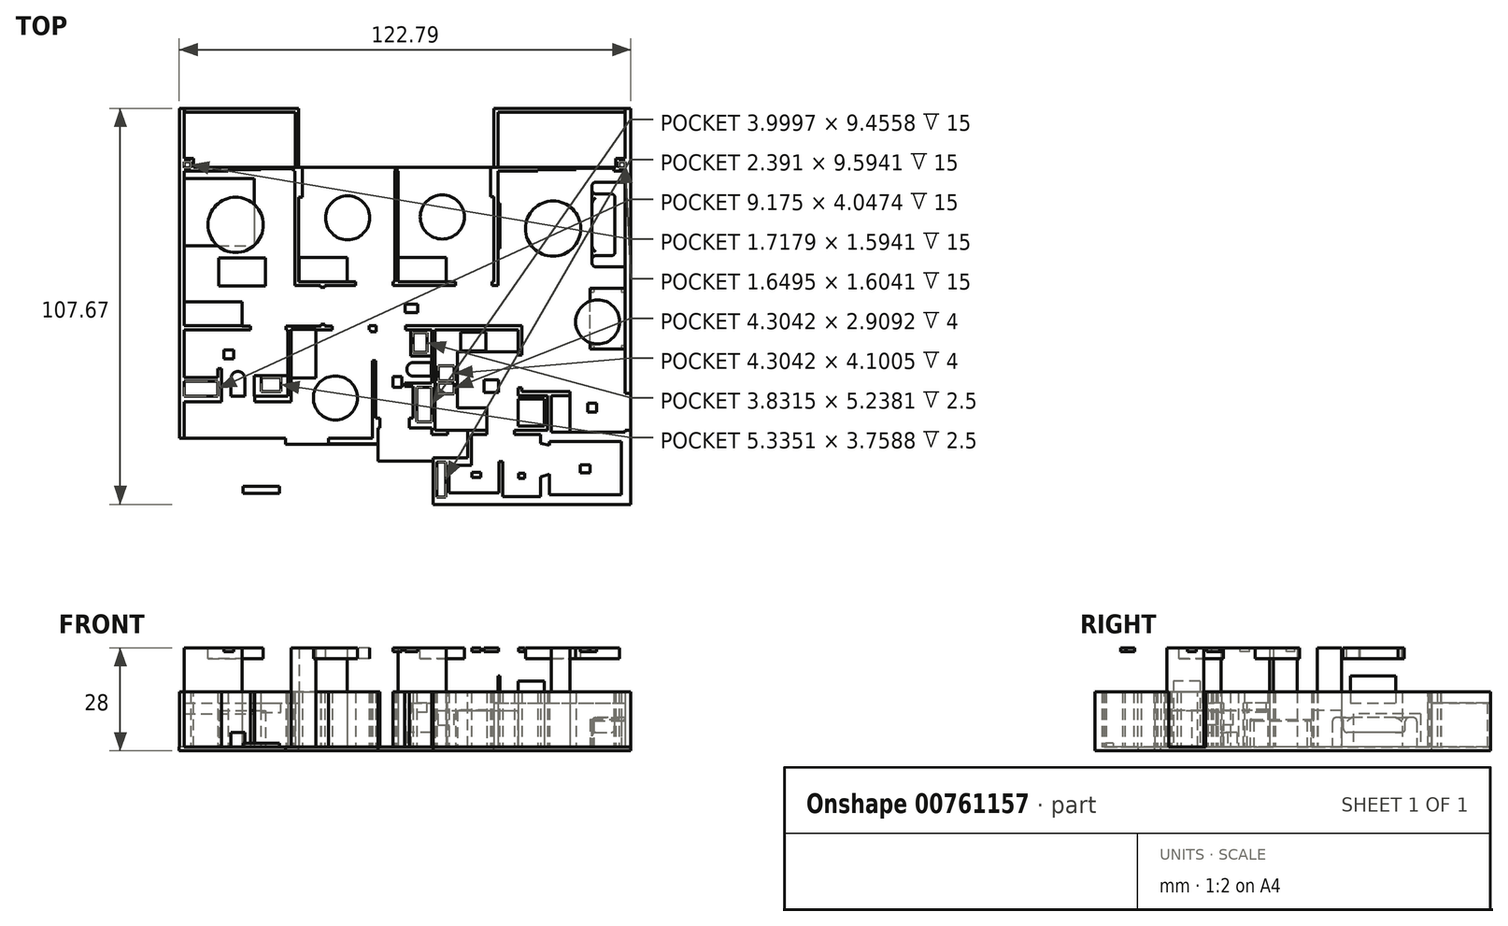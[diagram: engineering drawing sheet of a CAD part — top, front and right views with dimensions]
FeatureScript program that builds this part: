
annotation { "Feature Type Name" : "Feature", "Feature Type Description" : "" }
export const myFeature = defineFeature(function(context is Context, id is Id, definition is map)
    precondition{}
    {
        {
            var Q0;
            Q0=qCreatedBy(makeId("Top.planeOp"),FACE);
            var sketch = newSketch(context, id + "F0", { "sketchPlane" : qUnion([Q0])});
            skLineSegment(sketch, "E0.bottom", {"start": v(-44.07, -48.97) * mm, "end": v(-34.07, -48.97) * mm});
            skLineSegment(sketch, "E0.top", {"start": v(-44.07, -50.97) * mm, "end": v(-34.07, -50.97) * mm});
            skLineSegment(sketch, "E0.left", {"start": v(-44.07, -48.97) * mm, "end": v(-44.07, -50.97) * mm});
            skLineSegment(sketch, "E0.right", {"start": v(-34.07, -48.97) * mm, "end": v(-34.07, -50.97) * mm});
            skSolve(sketch);
        }
        {
            var Q0;
            Q0 = qSketchRegion(id + "F0", true);
            extrude(context, id + "F1", {"entities" : qUnion([Q0]), "depth" : 1 * mm, "offsetDistance" : 25 * mm});
        }
        {
            var Q0;
            Q0=qCreatedBy(makeId("Top.planeOp"),FACE);
            var sketch = newSketch(context, id + "F2", { "sketchPlane" : qUnion([Q0])});
            skLineSegment(sketch, "E1", {"start": v(-61.37, 53.72) * mm, "end": v(-61.37, -35.97) * mm});
            skLineSegment(sketch, "E2", {"start": v(-61.37, -35.97) * mm, "end": v(-32.45, -35.97) * mm});
            skLineSegment(sketch, "E3", {"start": v(-32.45, -35.97) * mm, "end": v(-32.45, -37.62) * mm});
            skLineSegment(sketch, "E4", {"start": v(-32.45, -37.62) * mm, "end": v(-7.36, -37.62) * mm});
            skLineSegment(sketch, "E5", {"start": v(-7.36, -37.62) * mm, "end": v(-7.36, -42.12) * mm});
            skLineSegment(sketch, "E6", {"start": v(-7.36, -42.12) * mm, "end": v(7.72, -42.12) * mm});
            skLineSegment(sketch, "E7", {"start": v(7.72, -42.12) * mm, "end": v(7.72, -53.92) * mm});
            skLineSegment(sketch, "E8", {"start": v(7.72, -53.92) * mm, "end": v(61.42, -53.92) * mm});
            skLineSegment(sketch, "E9", {"start": v(61.42, -53.92) * mm, "end": v(61.42, 53.72) * mm});
            skLineSegment(sketch, "E10", {"start": v(61.42, 53.72) * mm, "end": v(24.18, 53.72) * mm});
            skLineSegment(sketch, "E11", {"start": v(24.18, 53.72) * mm, "end": v(24.18, 37.72) * mm});
            skLineSegment(sketch, "E12", {"start": v(24.18, 37.72) * mm, "end": v(-28.88, 37.72) * mm});
            skLineSegment(sketch, "E13", {"start": v(-28.88, 37.72) * mm, "end": v(-28.88, 53.72) * mm});
            skLineSegment(sketch, "E14", {"start": v(-28.88, 53.72) * mm, "end": v(-61.37, 53.72) * mm});
            skSolve(sketch);
        }
        {
            var Q0;
            Q0 = qSketchRegion(id + "F2", true);
            extrude(context, id + "F3", {"entities" : qUnion([Q0]), "oppositeDirection" : true, "depth" : 1 * mm, "offsetDistance" : 25 * mm});
        }
        {
            var Q0;
            Q0=qCreatedBy(makeId("Top.planeOp"),FACE);
            var sketch = newSketch(context, id + "F4", { "sketchPlane" : qUnion([Q0])});
            skLineSegment(sketch, "E15.bottom", {"start": v(-61.36, 53.74) * mm, "end": v(-60.03, 53.74) * mm});
            skLineSegment(sketch, "E15.top", {"start": v(-61.36, -35.96) * mm, "end": v(-60.03, -35.96) * mm});
            skLineSegment(sketch, "E15.left", {"start": v(-61.36, 53.74) * mm, "end": v(-61.36, -35.96) * mm});
            skLineSegment(sketch, "E15.right", {"start": v(-60.03, 53.74) * mm, "end": v(-60.03, -35.96) * mm});
            skLineSegment(sketch, "E16.bottom", {"start": v(-60.03, -24.49) * mm, "end": v(-49.92, -24.49) * mm});
            skLineSegment(sketch, "E16.top", {"start": v(-60.03, -25.96) * mm, "end": v(-49.92, -25.96) * mm});
            skLineSegment(sketch, "E16.left", {"start": v(-60.03, -24.49) * mm, "end": v(-60.03, -25.96) * mm});
            skLineSegment(sketch, "E16.right", {"start": v(-49.92, -24.49) * mm, "end": v(-49.92, -25.96) * mm});
            skLineSegment(sketch, "E17.bottom", {"start": v(-49.92, -24.49) * mm, "end": v(-50.86, -24.49) * mm});
            skLineSegment(sketch, "E17.top", {"start": v(-49.92, -17.05) * mm, "end": v(-50.86, -17.05) * mm});
            skLineSegment(sketch, "E17.left", {"start": v(-49.92, -24.49) * mm, "end": v(-49.92, -17.05) * mm});
            skLineSegment(sketch, "E17.right", {"start": v(-50.86, -24.49) * mm, "end": v(-50.86, -17.05) * mm});
            skLineSegment(sketch, "E18.bottom", {"start": v(-50.86, -19.45) * mm, "end": v(-60.03, -19.45) * mm});
            skLineSegment(sketch, "E18.top", {"start": v(-50.86, -20.44) * mm, "end": v(-60.03, -20.44) * mm});
            skLineSegment(sketch, "E18.left", {"start": v(-50.86, -19.45) * mm, "end": v(-50.86, -20.44) * mm});
            skLineSegment(sketch, "E18.right", {"start": v(-60.03, -19.45) * mm, "end": v(-60.03, -20.44) * mm});
            skLineSegment(sketch, "E19.bottom", {"start": v(-60.03, -5.39) * mm, "end": v(-41.95, -5.39) * mm});
            skLineSegment(sketch, "E19.top", {"start": v(-60.03, -6.43) * mm, "end": v(-41.95, -6.43) * mm});
            skLineSegment(sketch, "E19.left", {"start": v(-60.03, -5.39) * mm, "end": v(-60.03, -6.43) * mm});
            skLineSegment(sketch, "E19.right", {"start": v(-41.95, -5.39) * mm, "end": v(-41.95, -6.43) * mm});
            skLineSegment(sketch, "E20.bottom", {"start": v(-60.03, 39.23) * mm, "end": v(-57.5, 39.23) * mm});
            skLineSegment(sketch, "E20.top", {"start": v(-60.03, 40.15) * mm, "end": v(-57.5, 40.15) * mm});
            skLineSegment(sketch, "E20.left", {"start": v(-60.03, 39.23) * mm, "end": v(-60.03, 40.15) * mm});
            skLineSegment(sketch, "E20.right", {"start": v(-57.5, 39.23) * mm, "end": v(-57.5, 40.15) * mm});
            skLineSegment(sketch, "E21.bottom", {"start": v(-57.5, 39.23) * mm, "end": v(-58.31, 39.23) * mm});
            skLineSegment(sketch, "E21.top", {"start": v(-57.5, 36.71) * mm, "end": v(-58.31, 36.71) * mm});
            skLineSegment(sketch, "E21.left", {"start": v(-57.5, 39.23) * mm, "end": v(-57.5, 36.71) * mm});
            skLineSegment(sketch, "E21.right", {"start": v(-58.31, 39.23) * mm, "end": v(-58.31, 36.71) * mm});
            skLineSegment(sketch, "E22.bottom", {"start": v(-58.31, 36.71) * mm, "end": v(-60.03, 36.71) * mm});
            skLineSegment(sketch, "E22.top", {"start": v(-58.31, 37.64) * mm, "end": v(-60.03, 37.64) * mm});
            skLineSegment(sketch, "E22.left", {"start": v(-58.31, 36.71) * mm, "end": v(-58.31, 37.64) * mm});
            skLineSegment(sketch, "E22.right", {"start": v(-60.03, 36.71) * mm, "end": v(-60.03, 37.64) * mm});
            skLineSegment(sketch, "E23.bottom", {"start": v(-29.88, 37.73) * mm, "end": v(-27.86, 37.73) * mm});
            skLineSegment(sketch, "E23.top", {"start": v(-29.88, 29.66) * mm, "end": v(-27.86, 29.66) * mm});
            skLineSegment(sketch, "E23.left", {"start": v(-29.88, 37.73) * mm, "end": v(-29.88, 29.66) * mm});
            skLineSegment(sketch, "E23.right", {"start": v(-27.86, 37.73) * mm, "end": v(-27.86, 29.66) * mm});
            skLineSegment(sketch, "E24.bottom", {"start": v(-28.87, 29.66) * mm, "end": v(-29.88, 29.66) * mm});
            skLineSegment(sketch, "E24.top", {"start": v(-28.87, 5.58) * mm, "end": v(-29.88, 5.58) * mm});
            skLineSegment(sketch, "E24.left", {"start": v(-28.87, 29.66) * mm, "end": v(-28.87, 5.58) * mm});
            skLineSegment(sketch, "E24.right", {"start": v(-29.88, 29.66) * mm, "end": v(-29.88, 5.58) * mm});
            skLineSegment(sketch, "E25.bottom", {"start": v(-28.87, 5.58) * mm, "end": v(-13.36, 5.58) * mm});
            skLineSegment(sketch, "E25.top", {"start": v(-28.87, 6.6) * mm, "end": v(-13.36, 6.6) * mm});
            skLineSegment(sketch, "E25.left", {"start": v(-28.87, 5.58) * mm, "end": v(-28.87, 6.6) * mm});
            skLineSegment(sketch, "E25.right", {"start": v(-13.36, 5.58) * mm, "end": v(-13.36, 6.6) * mm});
            skLineSegment(sketch, "E26.bottom", {"start": v(-22.9, 5.1) * mm, "end": v(-21.8, 5.1) * mm});
            skLineSegment(sketch, "E26.top", {"start": v(-22.9, 5.58) * mm, "end": v(-21.8, 5.58) * mm});
            skLineSegment(sketch, "E26.left", {"start": v(-22.9, 5.1) * mm, "end": v(-22.9, 5.58) * mm});
            skLineSegment(sketch, "E26.right", {"start": v(-21.8, 5.1) * mm, "end": v(-21.8, 5.58) * mm});
            skLineSegment(sketch, "E27.bottom", {"start": v(-2.78, 36.67) * mm, "end": v(-1.84, 36.67) * mm});
            skLineSegment(sketch, "E27.top", {"start": v(-2.78, 5.61) * mm, "end": v(-1.84, 5.61) * mm});
            skLineSegment(sketch, "E27.left", {"start": v(-2.78, 36.67) * mm, "end": v(-2.78, 5.61) * mm});
            skLineSegment(sketch, "E27.right", {"start": v(-1.84, 36.67) * mm, "end": v(-1.84, 5.61) * mm});
            skLineSegment(sketch, "E28.bottom", {"start": v(-3.28, 5.61) * mm, "end": v(13.72, 5.61) * mm});
            skLineSegment(sketch, "E28.top", {"start": v(-3.28, 6.64) * mm, "end": v(13.72, 6.64) * mm});
            skLineSegment(sketch, "E28.left", {"start": v(-3.28, 5.61) * mm, "end": v(-3.28, 6.64) * mm});
            skLineSegment(sketch, "E28.right", {"start": v(13.72, 5.61) * mm, "end": v(13.72, 6.64) * mm});
            skLineSegment(sketch, "E29.bottom", {"start": v(-2.59, 37.73) * mm, "end": v(-2.14, 37.73) * mm});
            skLineSegment(sketch, "E29.top", {"start": v(-2.59, 36.67) * mm, "end": v(-2.14, 36.67) * mm});
            skLineSegment(sketch, "E29.left", {"start": v(-2.59, 37.73) * mm, "end": v(-2.59, 36.67) * mm});
            skLineSegment(sketch, "E29.right", {"start": v(-2.14, 37.73) * mm, "end": v(-2.14, 36.67) * mm});
            skLineSegment(sketch, "E30.bottom", {"start": v(25.3, 37.74) * mm, "end": v(23.25, 37.74) * mm});
            skLineSegment(sketch, "E30.top", {"start": v(25.3, 29.67) * mm, "end": v(23.25, 29.67) * mm});
            skLineSegment(sketch, "E30.left", {"start": v(25.3, 37.74) * mm, "end": v(25.3, 29.67) * mm});
            skLineSegment(sketch, "E30.right", {"start": v(23.25, 37.74) * mm, "end": v(23.25, 29.67) * mm});
            skLineSegment(sketch, "E31.bottom", {"start": v(25.3, 29.67) * mm, "end": v(24.22, 29.67) * mm});
            skLineSegment(sketch, "E31.top", {"start": v(25.3, 5.57) * mm, "end": v(24.22, 5.57) * mm});
            skLineSegment(sketch, "E31.left", {"start": v(25.3, 29.67) * mm, "end": v(25.3, 5.57) * mm});
            skLineSegment(sketch, "E31.right", {"start": v(24.22, 29.67) * mm, "end": v(24.22, 5.57) * mm});
            skLineSegment(sketch, "E32.bottom", {"start": v(24.22, 5.57) * mm, "end": v(23.72, 5.57) * mm});
            skLineSegment(sketch, "E32.top", {"start": v(24.22, 6.61) * mm, "end": v(23.72, 6.61) * mm});
            skLineSegment(sketch, "E32.left", {"start": v(24.22, 5.57) * mm, "end": v(24.22, 6.61) * mm});
            skLineSegment(sketch, "E32.right", {"start": v(23.72, 5.57) * mm, "end": v(23.72, 6.61) * mm});
            skLineSegment(sketch, "E33.bottom", {"start": v(61.42, 53.73) * mm, "end": v(59.89, 53.73) * mm});
            skLineSegment(sketch, "E33.top", {"start": v(61.42, -23.72) * mm, "end": v(59.89, -23.72) * mm});
            skLineSegment(sketch, "E33.left", {"start": v(61.42, 53.73) * mm, "end": v(61.42, -23.72) * mm});
            skLineSegment(sketch, "E33.right", {"start": v(59.89, 53.73) * mm, "end": v(59.89, -23.72) * mm});
            skLineSegment(sketch, "E34.bottom", {"start": v(59.89, 40.2) * mm, "end": v(57.36, 40.2) * mm});
            skLineSegment(sketch, "E34.top", {"start": v(59.89, 39.23) * mm, "end": v(57.36, 39.23) * mm});
            skLineSegment(sketch, "E34.left", {"start": v(59.89, 40.2) * mm, "end": v(59.89, 39.23) * mm});
            skLineSegment(sketch, "E34.right", {"start": v(57.36, 40.2) * mm, "end": v(57.36, 39.23) * mm});
            skLineSegment(sketch, "E35.bottom", {"start": v(57.36, 39.23) * mm, "end": v(58.24, 39.23) * mm});
            skLineSegment(sketch, "E35.top", {"start": v(57.36, 36.68) * mm, "end": v(58.24, 36.68) * mm});
            skLineSegment(sketch, "E35.left", {"start": v(57.36, 39.23) * mm, "end": v(57.36, 36.68) * mm});
            skLineSegment(sketch, "E35.right", {"start": v(58.24, 39.23) * mm, "end": v(58.24, 36.68) * mm});
            skLineSegment(sketch, "E36.bottom", {"start": v(58.24, 36.68) * mm, "end": v(59.89, 36.68) * mm});
            skLineSegment(sketch, "E36.top", {"start": v(58.24, 37.62) * mm, "end": v(59.89, 37.62) * mm});
            skLineSegment(sketch, "E36.left", {"start": v(58.24, 36.68) * mm, "end": v(58.24, 37.62) * mm});
            skLineSegment(sketch, "E36.right", {"start": v(59.89, 36.68) * mm, "end": v(59.89, 37.62) * mm});
            skLineSegment(sketch, "E37.bottom", {"start": v(61.42, -53.9) * mm, "end": v(36.84, -53.9) * mm});
            skLineSegment(sketch, "E37.top", {"start": v(61.42, -51.34) * mm, "end": v(36.84, -51.34) * mm});
            skLineSegment(sketch, "E37.left", {"start": v(61.42, -53.9) * mm, "end": v(61.42, -51.34) * mm});
            skLineSegment(sketch, "E37.right", {"start": v(36.84, -53.9) * mm, "end": v(36.84, -51.34) * mm});
            skLineSegment(sketch, "E38.bottom", {"start": v(61.42, -51.34) * mm, "end": v(58.83, -51.34) * mm});
            skLineSegment(sketch, "E38.top", {"start": v(61.42, -34.3) * mm, "end": v(58.83, -34.3) * mm});
            skLineSegment(sketch, "E38.left", {"start": v(61.42, -51.34) * mm, "end": v(61.42, -34.3) * mm});
            skLineSegment(sketch, "E38.right", {"start": v(58.83, -51.34) * mm, "end": v(58.83, -34.3) * mm});
            skLineSegment(sketch, "E39.bottom", {"start": v(58.83, -34.3) * mm, "end": v(36.84, -34.3) * mm});
            skLineSegment(sketch, "E39.top", {"start": v(58.83, -36.83) * mm, "end": v(39.31, -36.83) * mm});
            skLineSegment(sketch, "E39.left", {"start": v(58.83, -34.3) * mm, "end": v(58.83, -36.83) * mm});
            skLineSegment(sketch, "E39.right", {"start": v(36.84, -34.3) * mm, "end": v(36.84, -36.83) * mm});
            skLineSegment(sketch, "E40.top", {"start": v(36.84, -51.34) * mm, "end": v(39.32, -51.34) * mm});
            skLineSegment(sketch, "E40.left", {"start": v(36.84, -46.44) * mm, "end": v(36.84, -51.34) * mm});
            skLineSegment(sketch, "E40.right", {"start": v(39.32, -46.44) * mm, "end": v(39.32, -51.34) * mm});
            skLineSegment(sketch, "E41", {"start": v(36.84, -36.83) * mm, "end": v(36.84, -37.28) * mm});
            skLineSegment(sketch, "E42", {"start": v(36.84, -37.28) * mm, "end": v(39.31, -37.83) * mm});
            skLineSegment(sketch, "E43", {"start": v(39.31, -37.83) * mm, "end": v(39.31, -36.83) * mm});
            skLineSegment(sketch, "E44", {"start": v(39.32, -45.73) * mm, "end": v(39.32, -46.44) * mm});
            skLineSegment(sketch, "E45", {"start": v(39.32, -45.73) * mm, "end": v(36.84, -46.44) * mm});
            skLineSegment(sketch, "E46", {"start": v(30.74, -22.23) * mm, "end": v(30.74, -24.32) * mm});
            skLineSegment(sketch, "E47", {"start": v(30.74, -24.32) * mm, "end": v(38.83, -24.32) * mm});
            skLineSegment(sketch, "E48", {"start": v(38.83, -24.32) * mm, "end": v(38.83, -33.76) * mm});
            skLineSegment(sketch, "E49", {"start": v(38.83, -33.76) * mm, "end": v(29.77, -33.76) * mm});
            skLineSegment(sketch, "E50", {"start": v(29.77, -33.76) * mm, "end": v(29.77, -34.86) * mm});
            skLineSegment(sketch, "E51", {"start": v(29.77, -34.86) * mm, "end": v(36.84, -34.86) * mm});
            skLineSegment(sketch, "E52", {"start": v(39.82, -34.3) * mm, "end": v(39.82, -24.32) * mm});
            skLineSegment(sketch, "E53", {"start": v(39.82, -24.32) * mm, "end": v(44.86, -24.32) * mm});
            skLineSegment(sketch, "E54", {"start": v(44.86, -24.32) * mm, "end": v(44.86, -23.17) * mm});
            skLineSegment(sketch, "E55", {"start": v(44.86, -23.17) * mm, "end": v(31.78, -23.17) * mm});
            skLineSegment(sketch, "E56", {"start": v(31.78, -23.17) * mm, "end": v(31.78, -22.2) * mm});
            skLineSegment(sketch, "E57", {"start": v(31.78, -22.2) * mm, "end": v(30.74, -22.23) * mm});
            skLineSegment(sketch, "E58", {"start": v(59.86, -33.79) * mm, "end": v(59.86, -34.3) * mm});
            skLineSegment(sketch, "E59", {"start": v(59.86, -34.3) * mm, "end": v(61.42, -34.3) * mm});
            skLineSegment(sketch, "E60", {"start": v(59.86, -33.79) * mm, "end": v(61.42, -33.79) * mm});
            skLineSegment(sketch, "E61", {"start": v(61.42, -33.79) * mm, "end": v(61.42, -34.3) * mm});
            skLineSegment(sketch, "E62", {"start": v(36.84, -53.9) * mm, "end": v(7.72, -53.9) * mm});
            skLineSegment(sketch, "E63", {"start": v(7.72, -53.9) * mm, "end": v(7.72, -41.29) * mm});
            skLineSegment(sketch, "E64", {"start": v(7.72, -41.29) * mm, "end": v(18.07, -41.29) * mm});
            skLineSegment(sketch, "E65", {"start": v(18.07, -41.29) * mm, "end": v(18.07, -43.28) * mm});
            skLineSegment(sketch, "E66", {"start": v(18.07, -43.28) * mm, "end": v(11.99, -43.28) * mm});
            skLineSegment(sketch, "E67", {"start": v(11.99, -43.28) * mm, "end": v(11.99, -50.82) * mm});
            skLineSegment(sketch, "E68", {"start": v(11.99, -50.82) * mm, "end": v(25.54, -50.82) * mm});
            skLineSegment(sketch, "E69", {"start": v(25.54, -50.82) * mm, "end": v(25.54, -42.28) * mm});
            skLineSegment(sketch, "E70", {"start": v(25.54, -42.28) * mm, "end": v(26.54, -42.28) * mm});
            skLineSegment(sketch, "E71", {"start": v(26.54, -42.28) * mm, "end": v(26.54, -51.82) * mm});
            skLineSegment(sketch, "E72", {"start": v(26.54, -51.82) * mm, "end": v(36.84, -51.82) * mm});
            skLineSegment(sketch, "E73.bottom", {"start": v(8.66, -42.35) * mm, "end": v(11.05, -42.35) * mm});
            skLineSegment(sketch, "E73.top", {"start": v(8.66, -51.94) * mm, "end": v(11.05, -51.94) * mm});
            skLineSegment(sketch, "E73.left", {"start": v(8.66, -42.35) * mm, "end": v(8.66, -51.94) * mm});
            skLineSegment(sketch, "E73.right", {"start": v(11.05, -42.35) * mm, "end": v(11.05, -51.94) * mm});
            skLineSegment(sketch, "E74.bottom", {"start": v(18.07, -41.29) * mm, "end": v(17, -41.29) * mm});
            skLineSegment(sketch, "E74.top", {"start": v(18.07, -34.9) * mm, "end": v(17, -34.9) * mm});
            skLineSegment(sketch, "E74.left", {"start": v(18.07, -41.29) * mm, "end": v(18.07, -34.9) * mm});
            skLineSegment(sketch, "E74.right", {"start": v(17, -41.29) * mm, "end": v(17, -34.9) * mm});
            skLineSegment(sketch, "E75.bottom", {"start": v(17, -34.9) * mm, "end": v(22.26, -34.9) * mm});
            skLineSegment(sketch, "E75.top", {"start": v(17, -33.79) * mm, "end": v(22.26, -33.79) * mm});
            skLineSegment(sketch, "E75.left", {"start": v(17, -34.9) * mm, "end": v(17, -33.79) * mm});
            skLineSegment(sketch, "E75.right", {"start": v(22.26, -34.9) * mm, "end": v(22.26, -33.79) * mm});
            skLineSegment(sketch, "E76.bottom", {"start": v(11.7, -33.79) * mm, "end": v(7.22, -33.79) * mm});
            skLineSegment(sketch, "E76.top", {"start": v(11.7, -34.9) * mm, "end": v(7.22, -34.9) * mm});
            skLineSegment(sketch, "E76.left", {"start": v(11.7, -33.79) * mm, "end": v(11.7, -34.9) * mm});
            skLineSegment(sketch, "E76.right", {"start": v(7.22, -33.79) * mm, "end": v(7.22, -34.9) * mm});
            skLineSegment(sketch, "E77.bottom", {"start": v(7.22, -33.79) * mm, "end": v(8.18, -33.79) * mm});
            skLineSegment(sketch, "E77.top", {"start": v(7.22, -6.42) * mm, "end": v(8.18, -6.42) * mm});
            skLineSegment(sketch, "E77.left", {"start": v(7.22, -33.79) * mm, "end": v(7.22, -6.42) * mm});
            skLineSegment(sketch, "E77.right", {"start": v(8.18, -33.79) * mm, "end": v(8.18, -6.42) * mm});
            skLineSegment(sketch, "E78.bottom", {"start": v(1.22, -33.12) * mm, "end": v(3.22, -33.12) * mm});
            skLineSegment(sketch, "E78.top", {"start": v(1.22, -30.48) * mm, "end": v(3.22, -30.48) * mm});
            skLineSegment(sketch, "E78.right", {"start": v(3.22, -33.12) * mm, "end": v(3.22, -30.48) * mm});
            skLineSegment(sketch, "E79.bottom", {"start": v(3.22, -33.12) * mm, "end": v(7.22, -33.12) * mm});
            skLineSegment(sketch, "E79.top", {"start": v(3.22, -31.51) * mm, "end": v(7.22, -31.51) * mm});
            skLineSegment(sketch, "E79.left", {"start": v(3.22, -33.12) * mm, "end": v(3.22, -31.51) * mm});
            skLineSegment(sketch, "E79.right", {"start": v(7.22, -33.12) * mm, "end": v(7.22, -31.51) * mm});
            skLineSegment(sketch, "E80.bottom", {"start": v(3.22, -30.48) * mm, "end": v(2.22, -30.48) * mm});
            skLineSegment(sketch, "E80.top", {"start": v(3.22, -20.95) * mm, "end": v(2.22, -20.95) * mm});
            skLineSegment(sketch, "E80.left", {"start": v(3.22, -30.48) * mm, "end": v(3.22, -20.95) * mm});
            skLineSegment(sketch, "E80.right", {"start": v(2.22, -30.48) * mm, "end": v(2.22, -20.95) * mm});
            skLineSegment(sketch, "E81.bottom", {"start": v(2.22, -20.95) * mm, "end": v(-0.09, -20.95) * mm});
            skLineSegment(sketch, "E81.top", {"start": v(2.22, -21.8) * mm, "end": v(-0.09, -21.8) * mm});
            skLineSegment(sketch, "E81.left", {"start": v(2.22, -20.95) * mm, "end": v(2.22, -21.8) * mm});
            skLineSegment(sketch, "E81.right", {"start": v(-0.09, -20.95) * mm, "end": v(-0.09, -21.8) * mm});
            skLineSegment(sketch, "E82.bottom", {"start": v(3.22, -20.95) * mm, "end": v(7.22, -20.95) * mm});
            skLineSegment(sketch, "E82.top", {"start": v(3.22, -22.06) * mm, "end": v(7.22, -22.06) * mm});
            skLineSegment(sketch, "E82.left", {"start": v(3.22, -20.95) * mm, "end": v(3.22, -22.06) * mm});
            skLineSegment(sketch, "E82.right", {"start": v(7.22, -20.95) * mm, "end": v(7.22, -22.06) * mm});
            skLineSegment(sketch, "E83.bottom", {"start": v(-20.85, -35.99) * mm, "end": v(-7.33, -35.99) * mm});
            skLineSegment(sketch, "E83.top", {"start": v(-20.85, -37.51) * mm, "end": v(-7.33, -37.51) * mm});
            skLineSegment(sketch, "E83.left", {"start": v(-20.85, -35.99) * mm, "end": v(-20.85, -37.51) * mm});
            skLineSegment(sketch, "E83.right", {"start": v(-7.33, -35.99) * mm, "end": v(-7.33, -37.51) * mm});
            skLineSegment(sketch, "E84.bottom", {"start": v(-8.91, -35.99) * mm, "end": v(-7.91, -35.99) * mm});
            skLineSegment(sketch, "E84.top", {"start": v(-8.91, -14.88) * mm, "end": v(-7.91, -14.88) * mm});
            skLineSegment(sketch, "E84.left", {"start": v(-8.91, -35.99) * mm, "end": v(-8.91, -14.88) * mm});
            skLineSegment(sketch, "E84.right", {"start": v(-7.91, -35.99) * mm, "end": v(-7.91, -14.88) * mm});
            skLineSegment(sketch, "E85", {"start": v(-7.91, -30.5) * mm, "end": v(-6.82, -30.5) * mm});
            skLineSegment(sketch, "E86", {"start": v(-6.82, -33.13) * mm, "end": v(-7.3, -33.13) * mm});
            skLineSegment(sketch, "E87", {"start": v(-7.3, -33.13) * mm, "end": v(-7.33, -35.99) * mm});
            skLineSegment(sketch, "E88.bottom", {"start": v(0.19, -5.32) * mm, "end": v(31.75, -5.32) * mm});
            skLineSegment(sketch, "E88.top", {"start": v(0.19, -6.42) * mm, "end": v(31.75, -6.42) * mm});
            skLineSegment(sketch, "E88.left", {"start": v(0.19, -5.32) * mm, "end": v(0.19, -6.42) * mm});
            skLineSegment(sketch, "E88.right", {"start": v(31.75, -5.32) * mm, "end": v(31.75, -6.42) * mm});
            skLineSegment(sketch, "E89.bottom", {"start": v(31.75, -6.4) * mm, "end": v(30.79, -6.4) * mm});
            skLineSegment(sketch, "E89.top", {"start": v(31.75, -13.26) * mm, "end": v(30.79, -13.26) * mm});
            skLineSegment(sketch, "E89.left", {"start": v(31.75, -6.4) * mm, "end": v(31.75, -13.26) * mm});
            skLineSegment(sketch, "E89.right", {"start": v(30.79, -6.4) * mm, "end": v(30.79, -13.26) * mm});
            skLineSegment(sketch, "E90.bottom", {"start": v(-40.94, -24.47) * mm, "end": v(-30.91, -24.47) * mm});
            skLineSegment(sketch, "E90.top", {"start": v(-40.94, -25.96) * mm, "end": v(-30.91, -25.96) * mm});
            skLineSegment(sketch, "E90.left", {"start": v(-40.94, -24.47) * mm, "end": v(-40.94, -25.96) * mm});
            skLineSegment(sketch, "E90.right", {"start": v(-30.91, -24.47) * mm, "end": v(-30.91, -25.96) * mm});
            skLineSegment(sketch, "E91.bottom", {"start": v(-30.91, -24.47) * mm, "end": v(-31.79, -24.47) * mm});
            skLineSegment(sketch, "E91.top", {"start": v(-30.91, -5.41) * mm, "end": v(-31.79, -5.41) * mm});
            skLineSegment(sketch, "E91.left", {"start": v(-30.91, -24.47) * mm, "end": v(-30.91, -5.41) * mm});
            skLineSegment(sketch, "E91.right", {"start": v(-31.79, -24.47) * mm, "end": v(-31.79, -5.41) * mm});
            skLineSegment(sketch, "E92.bottom", {"start": v(-32.38, -5.41) * mm, "end": v(-19.83, -5.41) * mm});
            skLineSegment(sketch, "E92.top", {"start": v(-32.38, -6.42) * mm, "end": v(-19.83, -6.42) * mm});
            skLineSegment(sketch, "E92.left", {"start": v(-32.38, -5.41) * mm, "end": v(-32.38, -6.42) * mm});
            skLineSegment(sketch, "E92.right", {"start": v(-19.83, -5.41) * mm, "end": v(-19.83, -6.42) * mm});
            skLineSegment(sketch, "E93.bottom", {"start": v(-21.8, -4.92) * mm, "end": v(-22.87, -4.92) * mm});
            skLineSegment(sketch, "E93.top", {"start": v(-21.8, -5.41) * mm, "end": v(-22.87, -5.41) * mm});
            skLineSegment(sketch, "E93.left", {"start": v(-21.8, -4.92) * mm, "end": v(-21.8, -5.41) * mm});
            skLineSegment(sketch, "E93.right", {"start": v(-22.87, -4.92) * mm, "end": v(-22.87, -5.41) * mm});
            skLineSegment(sketch, "E94", {"start": v(-7.89, -5.32) * mm, "end": v(-9.8, -5.32) * mm});
            skLineSegment(sketch, "E95", {"start": v(-9.8, -5.32) * mm, "end": v(-9.8, -6.44) * mm});
            skLineSegment(sketch, "E96", {"start": v(-9.8, -6.44) * mm, "end": v(-9.34, -6.44) * mm});
            skLineSegment(sketch, "E97", {"start": v(-9.34, -6.44) * mm, "end": v(-9.34, -6.95) * mm});
            skLineSegment(sketch, "E98", {"start": v(-9.34, -6.95) * mm, "end": v(-7.89, -6.95) * mm});
            skLineSegment(sketch, "E99", {"start": v(-7.89, -6.95) * mm, "end": v(-7.89, -5.32) * mm});
            skLineSegment(sketch, "E100.bottom", {"start": v(-20.85, -37.51) * mm, "end": v(-32.37, -37.51) * mm});
            skLineSegment(sketch, "E100.top", {"start": v(-20.85, -35.99) * mm, "end": v(-30.91, -35.99) * mm});
            skLineSegment(sketch, "E100.left", {"start": v(-20.85, -37.51) * mm, "end": v(-20.85, -35.99) * mm});
            skLineSegment(sketch, "E100.right", {"start": v(-32.37, -37.51) * mm, "end": v(-32.37, -35.99) * mm});
            skLineSegment(sketch, "E101.top", {"start": v(-32.37, -25.96) * mm, "end": v(-30.91, -25.96) * mm});
            skLineSegment(sketch, "E101.left", {"start": v(-32.37, -35.99) * mm, "end": v(-32.37, -25.96) * mm});
            skLineSegment(sketch, "E101.right", {"start": v(-30.91, -35.99) * mm, "end": v(-30.91, -25.96) * mm});
            skLineSegment(sketch, "E102", {"start": v(1.22, -30.48) * mm, "end": v(-6.82, -30.5) * mm});
            skLineSegment(sketch, "E103", {"start": v(-6.82, -33.13) * mm, "end": v(1.22, -33.12) * mm});
            skLineSegment(sketch, "E104.bottom", {"start": v(17, -33.79) * mm, "end": v(11.7, -33.79) * mm});
            skLineSegment(sketch, "E104.top", {"start": v(17, -34.9) * mm, "end": v(11.7, -34.9) * mm});
            skLineSegment(sketch, "E104.left", {"start": v(17, -33.79) * mm, "end": v(17, -34.9) * mm});
            skLineSegment(sketch, "E105.bottom", {"start": v(-40.94, -25.96) * mm, "end": v(-49.92, -25.96) * mm});
            skLineSegment(sketch, "E105.top", {"start": v(-40.94, -24.49) * mm, "end": v(-49.92, -24.49) * mm});
            skLineSegment(sketch, "E105.left", {"start": v(-40.94, -25.96) * mm, "end": v(-40.94, -24.49) * mm});
            skLineSegment(sketch, "E105.right", {"start": v(-49.92, -25.96) * mm, "end": v(-49.92, -24.49) * mm});
            skSolve(sketch);
        }
        {
            var Q0;
            Q0 = qSketchRegion(id + "F4", true);
            extrude(context, id + "F5", {"entities" : qUnion([Q0]), "operationType" : NewBodyOperationType.ADD, "depth" : 15 * mm, "offsetDistance" : 25 * mm});
        }
        {
            var Q0;
            Q0=qCreatedBy(makeId("Top.planeOp"),FACE);
            var sketch = newSketch(context, id + "F6", { "sketchPlane" : qUnion([Q0])});
            skLineSegment(sketch, "E106.bottom", {"start": v(-59.96, 53.75) * mm, "end": v(-28.88, 53.75) * mm});
            skLineSegment(sketch, "E106.top", {"start": v(-59.96, 52.76) * mm, "end": v(-28.88, 52.76) * mm});
            skLineSegment(sketch, "E106.left", {"start": v(-59.96, 53.75) * mm, "end": v(-59.96, 52.76) * mm});
            skLineSegment(sketch, "E106.right", {"start": v(-28.88, 53.75) * mm, "end": v(-28.88, 52.76) * mm});
            skLineSegment(sketch, "E107.bottom", {"start": v(-28.88, 52.76) * mm, "end": v(-29.85, 52.76) * mm});
            skLineSegment(sketch, "E107.top", {"start": v(-28.88, 37.7) * mm, "end": v(-29.85, 37.7) * mm});
            skLineSegment(sketch, "E107.left", {"start": v(-28.88, 52.76) * mm, "end": v(-28.88, 37.7) * mm});
            skLineSegment(sketch, "E107.right", {"start": v(-29.85, 52.76) * mm, "end": v(-29.85, 37.7) * mm});
            skLineSegment(sketch, "E108.bottom", {"start": v(24.16, 37.7) * mm, "end": v(25.3, 37.7) * mm});
            skLineSegment(sketch, "E108.top", {"start": v(24.16, 53.7) * mm, "end": v(25.3, 53.7) * mm});
            skLineSegment(sketch, "E108.left", {"start": v(24.16, 37.7) * mm, "end": v(24.16, 53.7) * mm});
            skLineSegment(sketch, "E108.right", {"start": v(25.3, 37.7) * mm, "end": v(25.3, 53.7) * mm});
            skLineSegment(sketch, "E109.bottom", {"start": v(25.3, 53.7) * mm, "end": v(59.87, 53.7) * mm});
            skLineSegment(sketch, "E109.top", {"start": v(25.3, 52.76) * mm, "end": v(59.87, 52.76) * mm});
            skLineSegment(sketch, "E109.left", {"start": v(25.3, 53.7) * mm, "end": v(25.3, 52.76) * mm});
            skLineSegment(sketch, "E109.right", {"start": v(59.87, 53.7) * mm, "end": v(59.87, 52.76) * mm});
            skSolve(sketch);
        }
        {
            var Q0;
            Q0 = qSketchRegion(id + "F6", true);
            extrude(context, id + "F7", {"entities" : qUnion([Q0]), "operationType" : NewBodyOperationType.ADD, "depth" : 12 * mm, "offsetDistance" : 25 * mm});
        }
        {
            var Q0;
            Q0=qCreatedBy(makeId("Top.planeOp"),FACE);
            var sketch = newSketch(context, id + "F8", { "sketchPlane" : qUnion([Q0])});
            skLineSegment(sketch, "E110", {"start": v(22.24, -33.76) * mm, "end": v(22.24, -27.64) * mm});
            skLineSegment(sketch, "E111", {"start": v(22.24, -27.64) * mm, "end": v(14.24, -27.64) * mm});
            skLineSegment(sketch, "E112", {"start": v(14.24, -27.64) * mm, "end": v(14.24, -12.45) * mm});
            skLineSegment(sketch, "E113", {"start": v(14.24, -12.45) * mm, "end": v(30.8, -12.45) * mm});
            skLineSegment(sketch, "E114", {"start": v(30.8, -12.45) * mm, "end": v(30.8, -6.41) * mm});
            skLineSegment(sketch, "E115", {"start": v(30.8, -6.41) * mm, "end": v(8.2, -6.41) * mm});
            skLineSegment(sketch, "E116", {"start": v(8.2, -6.41) * mm, "end": v(8.2, -33.76) * mm});
            skLineSegment(sketch, "E117", {"start": v(8.2, -33.76) * mm, "end": v(22.24, -33.76) * mm});
            skSolve(sketch);
        }
        {
            var Q0;
            Q0 = qSketchRegion(id + "F8", true);
            extrude(context, id + "F9", {"entities" : qUnion([Q0]), "operationType" : NewBodyOperationType.ADD, "depth" : 10 * mm, "offsetDistance" : 25 * mm});
        }
        {
            var Q0;
            Q0=qCreatedBy(makeId("Top.planeOp"),FACE);
            var sketch = newSketch(context, id + "F10", { "sketchPlane" : qUnion([Q0])});
            skLineSegment(sketch, "E118.bottom", {"start": v(37.9, -25.29) * mm, "end": v(30.73, -25.29) * mm});
            skLineSegment(sketch, "E118.top", {"start": v(37.9, -32.6) * mm, "end": v(30.73, -32.6) * mm});
            skLineSegment(sketch, "E118.left", {"start": v(37.9, -25.29) * mm, "end": v(37.9, -32.6) * mm});
            skLineSegment(sketch, "E118.right", {"start": v(30.73, -25.29) * mm, "end": v(30.73, -32.6) * mm});
            skSolve(sketch);
        }
        {
            var Q0;
            Q0 = qSketchRegion(id + "F10", true);
            extrude(context, id + "F11", {"entities" : qUnion([Q0]), "operationType" : NewBodyOperationType.ADD, "depth" : 18 * mm, "offsetDistance" : 25 * mm});
        }
        {
            var Q0;
            Q0=qCreatedBy(makeId("Top.planeOp"),FACE);
            var sketch = newSketch(context, id + "F12", { "sketchPlane" : qUnion([Q0])});
            skLineSegment(sketch, "E119.bottom", {"start": v(44.88, -24.31) * mm, "end": v(39.83, -24.31) * mm});
            skLineSegment(sketch, "E119.top", {"start": v(44.88, -34.3) * mm, "end": v(39.83, -34.3) * mm});
            skLineSegment(sketch, "E119.left", {"start": v(44.88, -24.31) * mm, "end": v(44.88, -34.3) * mm});
            skLineSegment(sketch, "E119.right", {"start": v(39.83, -24.31) * mm, "end": v(39.83, -34.3) * mm});
            skSolve(sketch);
        }
        {
            var Q0;
            Q0 = qSketchRegion(id + "F12", true);
            extrude(context, id + "F13", {"entities" : qUnion([Q0]), "operationType" : NewBodyOperationType.ADD, "depth" : 27 * mm, "offsetDistance" : 25 * mm});
        }
        {
            var Q0;
            Q0=qCreatedBy(makeId("Top.planeOp"),FACE);
            var sketch = newSketch(context, id + "F14", { "sketchPlane" : qUnion([Q0])});
            skLineSegment(sketch, "E120.bottom", {"start": v(-44.33, 1.17) * mm, "end": v(-60.03, 1.17) * mm});
            skLineSegment(sketch, "E120.top", {"start": v(-44.33, -5.38) * mm, "end": v(-60.03, -5.38) * mm});
            skLineSegment(sketch, "E120.left", {"start": v(-44.33, 1.17) * mm, "end": v(-44.33, -5.38) * mm});
            skLineSegment(sketch, "E120.right", {"start": v(-60.03, 1.17) * mm, "end": v(-60.03, -5.38) * mm});
            skLineSegment(sketch, "E121.bottom", {"start": v(-24.22, -19.59) * mm, "end": v(-30.92, -19.59) * mm});
            skLineSegment(sketch, "E121.top", {"start": v(-24.22, -6.4) * mm, "end": v(-30.92, -6.4) * mm});
            skLineSegment(sketch, "E121.left", {"start": v(-24.22, -19.59) * mm, "end": v(-24.22, -6.4) * mm});
            skLineSegment(sketch, "E121.right", {"start": v(-30.92, -19.59) * mm, "end": v(-30.92, -6.4) * mm});
            skLineSegment(sketch, "E122.bottom", {"start": v(-15.75, 13.18) * mm, "end": v(-28.84, 13.18) * mm});
            skLineSegment(sketch, "E122.top", {"start": v(-15.75, 6.58) * mm, "end": v(-28.84, 6.58) * mm});
            skLineSegment(sketch, "E122.left", {"start": v(-15.75, 13.18) * mm, "end": v(-15.75, 6.58) * mm});
            skLineSegment(sketch, "E122.right", {"start": v(-28.84, 13.18) * mm, "end": v(-28.84, 6.58) * mm});
            skLineSegment(sketch, "E123.bottom", {"start": v(11.27, 13.21) * mm, "end": v(-1.82, 13.21) * mm});
            skLineSegment(sketch, "E123.top", {"start": v(11.27, 6.58) * mm, "end": v(-1.82, 6.58) * mm});
            skLineSegment(sketch, "E123.left", {"start": v(11.27, 13.21) * mm, "end": v(11.27, 6.58) * mm});
            skLineSegment(sketch, "E123.right", {"start": v(-1.82, 13.21) * mm, "end": v(-1.82, 6.58) * mm});
            skSolve(sketch);
        }
        {
            var Q0;
            Q0 = qSketchRegion(id + "F14", true);
            extrude(context, id + "F15", {"entities" : qUnion([Q0]), "operationType" : NewBodyOperationType.ADD, "depth" : 27 * mm, "offsetDistance" : 25 * mm});
        }
        {
            var Q0;
            Q0=qCreatedBy(makeId("Top.planeOp"),FACE);
            var sketch = newSketch(context, id + "F16", { "sketchPlane" : qUnion([Q0])});
            skLineSegment(sketch, "E124.bottom", {"start": v(-60.03, 34.64) * mm, "end": v(-40.93, 34.64) * mm});
            skLineSegment(sketch, "E124.top", {"start": v(-60.03, 16.34) * mm, "end": v(-40.93, 16.34) * mm});
            skLineSegment(sketch, "E124.left", {"start": v(-60.03, 34.64) * mm, "end": v(-60.03, 16.34) * mm});
            skLineSegment(sketch, "E124.right", {"start": v(-40.93, 34.64) * mm, "end": v(-40.93, 16.34) * mm});
            skSolve(sketch);
        }
        {
            var Q0;
            Q0 = qSketchRegion(id + "F16", true);
            extrude(context, id + "F17", {"entities" : qUnion([Q0]), "operationType" : NewBodyOperationType.ADD, "depth" : 9 * mm, "offsetDistance" : 25 * mm});
        }
        {
            var Q0;
            Q0=makeQuery(id+"F9.opExtrude","CAP_FACE",FACE,{"disambiguationData":[OSD([sQuery(id+"F8.wireOp",EDGE,"E110"),sQuery(id+"F8.wireOp",EDGE,"E111"),sQuery(id+"F8.wireOp",EDGE,"E112"),sQuery(id+"F8.wireOp",EDGE,"E113"),sQuery(id+"F8.wireOp",EDGE,"E114"),sQuery(id+"F8.wireOp",EDGE,"E115"),sQuery(id+"F8.wireOp",EDGE,"E116"),sQuery(id+"F8.wireOp",EDGE,"E117")])],"isStart":false});
            var sketch = newSketch(context, id + "F18", { "sketchPlane" : qUnion([Q0])});
            skLineSegment(sketch, "E125.bottom", {"start": v(9.09, -16.22) * mm, "end": v(13.4, -16.22) * mm});
            skLineSegment(sketch, "E125.top", {"start": v(9.09, -23.83) * mm, "end": v(13.4, -23.83) * mm});
            skLineSegment(sketch, "E125.left", {"start": v(9.09, -16.22) * mm, "end": v(9.09, -20.32) * mm});
            skLineSegment(sketch, "E125.right", {"start": v(13.4, -16.22) * mm, "end": v(13.4, -23.83) * mm});
            skLineSegment(sketch, "E126", {"start": v(9.09, -20.92) * mm, "end": v(13.4, -20.92) * mm});
            skPoint(sketch, "E126.endSnap0", {"position": v(13.4, -20.03) * mm});
            skLineSegment(sketch, "E127", {"start": v(13.4, -20.32) * mm, "end": v(9.09, -20.32) * mm});
            skLineSegment(sketch, "E128.trimOffspring", {"start": v(9.09, -20.92) * mm, "end": v(9.09, -23.83) * mm});
            skSolve(sketch);
        }
        {
            var Q0;
            Q0 = qSketchRegion(id + "F18", true);
            extrude(context, id + "F19", {"entities" : qUnion([Q0]), "operationType" : NewBodyOperationType.REMOVE, "oppositeDirection" : true, "depth" : 4 * mm, "offsetDistance" : 25 * mm});
        }
        {
            var Q0;
            Q0=makeQuery(id+"F9.opExtrude","CAP_FACE",FACE,{"disambiguationData":[OSD([sQuery(id+"F8.wireOp",EDGE,"E110"),sQuery(id+"F8.wireOp",EDGE,"E111"),sQuery(id+"F8.wireOp",EDGE,"E112"),sQuery(id+"F8.wireOp",EDGE,"E113"),sQuery(id+"F8.wireOp",EDGE,"E114"),sQuery(id+"F8.wireOp",EDGE,"E115"),sQuery(id+"F8.wireOp",EDGE,"E116"),sQuery(id+"F8.wireOp",EDGE,"E117")])],"isStart":false});
            var sketch = newSketch(context, id + "F20", { "sketchPlane" : qUnion([Q0])});
            skLineSegment(sketch, "E129.bottom", {"start": v(15.2, -7.13) * mm, "end": v(22.03, -7.13) * mm});
            skLineSegment(sketch, "E129.top", {"start": v(15.2, -12.14) * mm, "end": v(22.03, -12.14) * mm});
            skLineSegment(sketch, "E129.left", {"start": v(15.2, -7.13) * mm, "end": v(15.2, -12.14) * mm});
            skLineSegment(sketch, "E129.right", {"start": v(22.03, -7.13) * mm, "end": v(22.03, -12.14) * mm});
            skSolve(sketch);
        }
        {
            var Q0;
            Q0=makeQuery(id+"F20.imprint","IMPRINT",FACE,{"disambiguationData":[TD([[makeQuery(id+"F20.imprint","IMPRINT",EDGE,{"derivedFrom":sQuery(id+"F20.wireOp",EDGE,"E129.bottom")}),-1.0]])]});
            extrude(context, id + "F21", {"entities" : qUnion([Q0]), "operationType" : NewBodyOperationType.ADD, "depth" : 0.2 * mm, "offsetDistance" : 25 * mm});
        }
        {
            var Q0;
            Q0=qCreatedBy(makeId("Top.planeOp"),FACE);
            var sketch = newSketch(context, id + "F22", { "sketchPlane" : qUnion([Q0])});
            skLineSegment(sketch, "E130.bottom", {"start": v(-56.94, 37.7) * mm, "end": v(-48.11, 37.7) * mm});
            skLineSegment(sketch, "E130.top", {"start": v(-56.94, 36.7) * mm, "end": v(-48.11, 36.7) * mm});
            skLineSegment(sketch, "E130.left", {"start": v(-56.94, 37.7) * mm, "end": v(-56.94, 36.7) * mm});
            skLineSegment(sketch, "E130.right", {"start": v(-48.11, 37.7) * mm, "end": v(-48.11, 36.7) * mm});
            skLineSegment(sketch, "E131.bottom", {"start": v(-48.11, 37.7) * mm, "end": v(-39.25, 37.7) * mm});
            skLineSegment(sketch, "E131.top", {"start": v(-48.11, 37.08) * mm, "end": v(-39.25, 37.08) * mm});
            skLineSegment(sketch, "E131.left", {"start": v(-48.11, 37.7) * mm, "end": v(-48.11, 37.08) * mm});
            skLineSegment(sketch, "E131.right", {"start": v(-39.25, 37.7) * mm, "end": v(-39.25, 37.08) * mm});
            skLineSegment(sketch, "E132.bottom", {"start": v(-39.25, 37.7) * mm, "end": v(-30.38, 37.7) * mm});
            skLineSegment(sketch, "E132.top", {"start": v(-39.25, 37.4) * mm, "end": v(-30.38, 37.4) * mm});
            skLineSegment(sketch, "E132.left", {"start": v(-39.25, 37.7) * mm, "end": v(-39.25, 37.4) * mm});
            skLineSegment(sketch, "E132.right", {"start": v(-30.38, 37.7) * mm, "end": v(-30.38, 37.4) * mm});
            skLineSegment(sketch, "E133.bottom", {"start": v(-30.38, 37.7) * mm, "end": v(-29.87, 37.7) * mm});
            skLineSegment(sketch, "E133.top", {"start": v(-30.38, 36.7) * mm, "end": v(-29.87, 36.7) * mm});
            skLineSegment(sketch, "E133.left", {"start": v(-30.38, 37.7) * mm, "end": v(-30.38, 36.7) * mm});
            skLineSegment(sketch, "E133.right", {"start": v(-29.87, 37.7) * mm, "end": v(-29.87, 36.7) * mm});
            skPoint(sketch, "E134.oppositeSnap0", {"position": v(-30.12, 36.7) * mm});
            skLineSegment(sketch, "E134.bottom", {"start": v(-56.94, 37.7) * mm, "end": v(-57.52, 37.7) * mm});
            skLineSegment(sketch, "E134.top", {"start": v(-56.94, 36.7) * mm, "end": v(-57.52, 36.7) * mm});
            skLineSegment(sketch, "E134.right", {"start": v(-57.52, 37.7) * mm, "end": v(-57.52, 36.7) * mm});
            skLineSegment(sketch, "E135.bottom", {"start": v(25.28, 37.75) * mm, "end": v(25.74, 37.75) * mm});
            skLineSegment(sketch, "E135.top", {"start": v(25.28, 36.66) * mm, "end": v(25.74, 36.66) * mm});
            skLineSegment(sketch, "E135.left", {"start": v(25.28, 37.75) * mm, "end": v(25.28, 36.66) * mm});
            skLineSegment(sketch, "E135.right", {"start": v(25.74, 37.75) * mm, "end": v(25.74, 36.66) * mm});
            skLineSegment(sketch, "E136.bottom", {"start": v(25.74, 36.66) * mm, "end": v(36.1, 36.66) * mm});
            skLineSegment(sketch, "E136.top", {"start": v(25.74, 37.7) * mm, "end": v(36.1, 37.7) * mm});
            skLineSegment(sketch, "E136.left", {"start": v(25.74, 36.66) * mm, "end": v(25.74, 37.7) * mm});
            skLineSegment(sketch, "E136.right", {"start": v(36.1, 36.66) * mm, "end": v(36.1, 37.7) * mm});
            skLineSegment(sketch, "E137.bottom", {"start": v(36.1, 37.7) * mm, "end": v(46.52, 37.7) * mm});
            skLineSegment(sketch, "E137.top", {"start": v(36.1, 37.07) * mm, "end": v(46.52, 37.07) * mm});
            skLineSegment(sketch, "E137.left", {"start": v(36.1, 37.7) * mm, "end": v(36.1, 37.07) * mm});
            skLineSegment(sketch, "E137.right", {"start": v(46.52, 37.7) * mm, "end": v(46.52, 37.07) * mm});
            skLineSegment(sketch, "E138.bottom", {"start": v(46.52, 37.7) * mm, "end": v(56.83, 37.7) * mm});
            skLineSegment(sketch, "E138.top", {"start": v(46.52, 37.45) * mm, "end": v(56.83, 37.45) * mm});
            skLineSegment(sketch, "E138.left", {"start": v(46.52, 37.7) * mm, "end": v(46.52, 37.45) * mm});
            skLineSegment(sketch, "E138.right", {"start": v(56.83, 37.7) * mm, "end": v(56.83, 37.45) * mm});
            skLineSegment(sketch, "E139.bottom", {"start": v(56.83, 37.7) * mm, "end": v(57.36, 37.7) * mm});
            skLineSegment(sketch, "E139.top", {"start": v(56.83, 36.69) * mm, "end": v(57.36, 36.69) * mm});
            skLineSegment(sketch, "E139.left", {"start": v(56.83, 37.7) * mm, "end": v(56.83, 36.69) * mm});
            skLineSegment(sketch, "E139.right", {"start": v(57.36, 37.7) * mm, "end": v(57.36, 36.69) * mm});
            skSolve(sketch);
        }
        {
            var Q0;
            Q0 = qSketchRegion(id + "F22", true);
            extrude(context, id + "F23", {"entities" : qUnion([Q0]), "operationType" : NewBodyOperationType.ADD, "depth" : 15 * mm, "offsetDistance" : 25 * mm});
        }
        {
            var Q0;
            Q0=qCreatedBy(makeId("Top.planeOp"),FACE);
            var sketch = newSketch(context, id + "F24", { "sketchPlane" : qUnion([Q0])});
            skLineSegment(sketch, "E140.bottom", {"start": v(50.39, 4.78) * mm, "end": v(51.39, 4.78) * mm});
            skLineSegment(sketch, "E140.top", {"start": v(50.39, 3.78) * mm, "end": v(51.39, 3.78) * mm});
            skLineSegment(sketch, "E140.left", {"start": v(50.39, 4.78) * mm, "end": v(50.39, 3.78) * mm});
            skLineSegment(sketch, "E140.right", {"start": v(51.39, 4.78) * mm, "end": v(51.39, 3.78) * mm});
            skLineSegment(sketch, "E141.bottom", {"start": v(58.89, 4.78) * mm, "end": v(59.89, 4.78) * mm});
            skLineSegment(sketch, "E141.top", {"start": v(58.89, 3.78) * mm, "end": v(59.89, 3.78) * mm});
            skLineSegment(sketch, "E141.left", {"start": v(58.89, 4.78) * mm, "end": v(58.89, 3.78) * mm});
            skLineSegment(sketch, "E141.right", {"start": v(59.89, 4.78) * mm, "end": v(59.89, 3.78) * mm});
            skLineSegment(sketch, "E142.bottom", {"start": v(59.89, -10.72) * mm, "end": v(58.89, -10.72) * mm});
            skLineSegment(sketch, "E142.top", {"start": v(59.89, -11.72) * mm, "end": v(58.89, -11.72) * mm});
            skLineSegment(sketch, "E142.left", {"start": v(59.89, -10.72) * mm, "end": v(59.89, -11.72) * mm});
            skLineSegment(sketch, "E142.right", {"start": v(58.89, -10.72) * mm, "end": v(58.89, -11.72) * mm});
            skLineSegment(sketch, "E143.bottom", {"start": v(51.39, -10.72) * mm, "end": v(50.39, -10.72) * mm});
            skLineSegment(sketch, "E143.top", {"start": v(51.39, -11.72) * mm, "end": v(50.39, -11.72) * mm});
            skLineSegment(sketch, "E143.left", {"start": v(51.39, -10.72) * mm, "end": v(51.39, -11.72) * mm});
            skLineSegment(sketch, "E143.right", {"start": v(50.39, -10.72) * mm, "end": v(50.39, -11.72) * mm});
            skSolve(sketch);
        }
        {
            var Q0;
            Q0 = qSketchRegion(id + "F24", true);
            extrude(context, id + "F25", {"entities" : qUnion([Q0]), "operationType" : NewBodyOperationType.ADD, "depth" : 7.2 * mm, "offsetDistance" : 25 * mm});
        }
        {
            var Q0;
            Q0=makeQuery(id+"F25.opExtrude","CAP_FACE",FACE,{"disambiguationData":[OSD([sQuery(id+"F24.wireOp",EDGE,"E143.bottom"),sQuery(id+"F24.wireOp",EDGE,"E143.top"),sQuery(id+"F24.wireOp",EDGE,"E143.left"),sQuery(id+"F24.wireOp",EDGE,"E143.right")])],"isStart":false});
            var sketch = newSketch(context, id + "F26", { "sketchPlane" : qUnion([Q0])});
            skLineSegment(sketch, "E144.bottom", {"start": v(50.89, -11.72) * mm, "end": v(59.39, -11.72) * mm});
            skLineSegment(sketch, "E144.top", {"start": v(50.89, 4.78) * mm, "end": v(59.39, 4.78) * mm});
            skLineSegment(sketch, "E144.left", {"start": v(50.39, -11.22) * mm, "end": v(50.39, 4.28) * mm});
            skLineSegment(sketch, "E144.right", {"start": v(59.89, -11.22) * mm, "end": v(59.89, 4.28) * mm});
            skPoint(sketch, "E145.visualSharp", {"position": v(50.39, 4.78) * mm});
            skArc(sketch, "E145.filletArc", {"start": v(50.89, 4.78) * mm, "mid": v(50.53, 4.63) * mm, "end": v(50.39, 4.28) * mm});
            skPoint(sketch, "E146.visualSharp", {"position": v(59.89, 4.78) * mm});
            skArc(sketch, "E146.filletArc", {"start": v(59.89, 4.28) * mm, "mid": v(59.74, 4.63) * mm, "end": v(59.39, 4.78) * mm});
            skPoint(sketch, "E147.visualSharp", {"position": v(59.89, -11.72) * mm});
            skArc(sketch, "E147.filletArc", {"start": v(59.39, -11.72) * mm, "mid": v(59.74, -11.57) * mm, "end": v(59.89, -11.22) * mm});
            skPoint(sketch, "E148.visualSharp", {"position": v(50.39, -11.72) * mm});
            skArc(sketch, "E148.filletArc", {"start": v(50.39, -11.22) * mm, "mid": v(50.53, -11.57) * mm, "end": v(50.89, -11.72) * mm});
            skSolve(sketch);
        }
        {
            var Q0;
            Q0 = qSketchRegion(id + "F26", true);
            extrude(context, id + "F27", {"entities" : qUnion([Q0]), "operationType" : NewBodyOperationType.ADD, "depth" : 0.4 * mm, "offsetDistance" : 25 * mm});
        }
        {
            var Q0;
            Q0=qCreatedBy(makeId("Top.planeOp"),FACE);
            var sketch = newSketch(context, id + "F28", { "sketchPlane" : qUnion([Q0])});
            skLineSegment(sketch, "E149.left", {"start": v(59.89, 33.68) * mm, "end": v(59.89, 10.68) * mm});
            skLineSegment(sketch, "E150.MirrorCS", {"start": v(59.89, 33.68) * mm, "end": v(51.89, 33.68) * mm});
            skLineSegment(sketch, "E151.MirrorCS", {"start": v(50.89, 32.68) * mm, "end": v(50.89, 11.68) * mm});
            skLineSegment(sketch, "E152.MirrorCS", {"start": v(59.89, 10.68) * mm, "end": v(51.89, 10.68) * mm});
            skPoint(sketch, "E153.visualSharp", {"position": v(50.89, 33.68) * mm});
            skArc(sketch, "E153.filletArc", {"start": v(51.89, 33.68) * mm, "mid": v(51.18, 33.4) * mm, "end": v(50.89, 32.68) * mm});
            skPoint(sketch, "E154.visualSharp", {"position": v(50.89, 10.68) * mm});
            skArc(sketch, "E154.filletArc", {"start": v(50.89, 11.68) * mm, "mid": v(51.18, 10.98) * mm, "end": v(51.89, 10.68) * mm});
            skSolve(sketch);
        }
        {
            var Q0;
            Q0 = qSketchRegion(id + "F28", true);
            extrude(context, id + "F29", {"entities" : qUnion([Q0]), "operationType" : NewBodyOperationType.ADD, "depth" : 8 * mm, "offsetDistance" : 25 * mm});
        }
        {
            var Q0;
            Q0=makeQuery(id+"F23.boolean.opBoolean","MERGE",FACE,{"derivedFrom":[makeQuery(id+"F15.boolean.opBoolean","MERGE",FACE,{"derivedFrom":[makeQuery(id+"F5.opExtrude","CAP_FACE",FACE,{"disambiguationData":[OSD([sQuery(id+"F4.wireOp",EDGE,"E23.bottom"),sQuery(id+"F4.wireOp",EDGE,"E23.top"),sQuery(id+"F4.wireOp",EDGE,"E23.left"),sQuery(id+"F4.wireOp",EDGE,"E23.right"),sQuery(id+"F4.wireOp",EDGE,"E24.top"),sQuery(id+"F4.wireOp",EDGE,"E24.left"),sQuery(id+"F4.wireOp",EDGE,"E24.right"),sQuery(id+"F4.wireOp",EDGE,"E25.bottom"),sQuery(id+"F4.wireOp",EDGE,"E25.top"),sQuery(id+"F4.wireOp",EDGE,"E25.right"),sQuery(id+"F4.wireOp",EDGE,"E26.bottom"),sQuery(id+"F4.wireOp",EDGE,"E26.left"),sQuery(id+"F4.wireOp",EDGE,"E26.right")])],"isStart":false}),makeQuery(id+"F15.opExtrude","CAP_FACE",FACE,{"disambiguationData":[OSD([sQuery(id+"F14.wireOp",EDGE,"E122.bottom"),sQuery(id+"F14.wireOp",EDGE,"E122.top"),sQuery(id+"F14.wireOp",EDGE,"E122.left"),sQuery(id+"F14.wireOp",EDGE,"E122.right")])],"isStart":false})]}),makeQuery(id+"F15.boolean.opBoolean","MERGE",FACE,{"derivedFrom":[makeQuery(id+"F13.boolean.opBoolean","MERGE",FACE,{"derivedFrom":[makeQuery(id+"F5.opExtrude","CAP_FACE",FACE,{"disambiguationData":[OSD([sQuery(id+"F4.wireOp",EDGE,"E15.bottom"),sQuery(id+"F4.wireOp",EDGE,"E15.top"),sQuery(id+"F4.wireOp",EDGE,"E15.left"),sQuery(id+"F4.wireOp",EDGE,"E15.right"),sQuery(id+"F4.wireOp",EDGE,"E16.bottom"),sQuery(id+"F4.wireOp",EDGE,"E16.top"),sQuery(id+"F4.wireOp",EDGE,"E17.top"),sQuery(id+"F4.wireOp",EDGE,"E17.left"),sQuery(id+"F4.wireOp",EDGE,"E17.right"),sQuery(id+"F4.wireOp",EDGE,"E18.bottom"),sQuery(id+"F4.wireOp",EDGE,"E18.top"),sQuery(id+"F4.wireOp",EDGE,"E19.bottom"),sQuery(id+"F4.wireOp",EDGE,"E19.top"),sQuery(id+"F4.wireOp",EDGE,"E19.right"),sQuery(id+"F4.wireOp",EDGE,"E20.bottom"),sQuery(id+"F4.wireOp",EDGE,"E20.top"),sQuery(id+"F4.wireOp",EDGE,"E20.right"),sQuery(id+"F4.wireOp",EDGE,"E21.top"),sQuery(id+"F4.wireOp",EDGE,"E21.left"),sQuery(id+"F4.wireOp",EDGE,"E21.right"),sQuery(id+"F4.wireOp",EDGE,"E22.bottom"),sQuery(id+"F4.wireOp",EDGE,"E22.top"),sQuery(id+"F4.wireOp",EDGE,"E37.bottom"),sQuery(id+"F4.wireOp",EDGE,"E37.top"),sQuery(id+"F4.wireOp",EDGE,"E37.left"),sQuery(id+"F4.wireOp",EDGE,"E37.right"),sQuery(id+"F4.wireOp",EDGE,"E38.top"),sQuery(id+"F4.wireOp",EDGE,"E38.left"),sQuery(id+"F4.wireOp",EDGE,"E38.right"),sQuery(id+"F4.wireOp",EDGE,"E39.bottom"),sQuery(id+"F4.wireOp",EDGE,"E39.top"),sQuery(id+"F4.wireOp",EDGE,"E39.right"),sQuery(id+"F4.wireOp",EDGE,"E40.left"),sQuery(id+"F4.wireOp",EDGE,"E40.right"),sQuery(id+"F4.wireOp",EDGE,"E41"),sQuery(id+"F4.wireOp",EDGE,"E42"),sQuery(id+"F4.wireOp",EDGE,"E43"),sQuery(id+"F4.wireOp",EDGE,"E44"),sQuery(id+"F4.wireOp",EDGE,"E45"),sQuery(id+"F4.wireOp",EDGE,"E46"),sQuery(id+"F4.wireOp",EDGE,"E47"),sQuery(id+"F4.wireOp",EDGE,"E48"),sQuery(id+"F4.wireOp",EDGE,"E49"),sQuery(id+"F4.wireOp",EDGE,"E50"),sQuery(id+"F4.wireOp",EDGE,"E51"),sQuery(id+"F4.wireOp",EDGE,"E52"),sQuery(id+"F4.wireOp",EDGE,"E53"),sQuery(id+"F4.wireOp",EDGE,"E54"),sQuery(id+"F4.wireOp",EDGE,"E55"),sQuery(id+"F4.wireOp",EDGE,"E56"),sQuery(id+"F4.wireOp",EDGE,"E57"),sQuery(id+"F4.wireOp",EDGE,"E58"),sQuery(id+"F4.wireOp",EDGE,"E60"),sQuery(id+"F4.wireOp",EDGE,"E61"),sQuery(id+"F4.wireOp",EDGE,"E62"),sQuery(id+"F4.wireOp",EDGE,"E63"),sQuery(id+"F4.wireOp",EDGE,"E64"),sQuery(id+"F4.wireOp",EDGE,"E65"),sQuery(id+"F4.wireOp",EDGE,"E66"),sQuery(id+"F4.wireOp",EDGE,"E67"),sQuery(id+"F4.wireOp",EDGE,"E68"),sQuery(id+"F4.wireOp",EDGE,"E69"),sQuery(id+"F4.wireOp",EDGE,"E70"),sQuery(id+"F4.wireOp",EDGE,"E71"),sQuery(id+"F4.wireOp",EDGE,"E72"),sQuery(id+"F4.wireOp",EDGE,"E73.bottom"),sQuery(id+"F4.wireOp",EDGE,"E73.top"),sQuery(id+"F4.wireOp",EDGE,"E73.left"),sQuery(id+"F4.wireOp",EDGE,"E73.right"),sQuery(id+"F4.wireOp",EDGE,"E74.left"),sQuery(id+"F4.wireOp",EDGE,"E74.right"),sQuery(id+"F4.wireOp",EDGE,"E75.bottom"),sQuery(id+"F4.wireOp",EDGE,"E75.top"),sQuery(id+"F4.wireOp",EDGE,"E75.right"),sQuery(id+"F4.wireOp",EDGE,"E76.bottom"),sQuery(id+"F4.wireOp",EDGE,"E76.top"),sQuery(id+"F4.wireOp",EDGE,"E76.right"),sQuery(id+"F4.wireOp",EDGE,"E77.left"),sQuery(id+"F4.wireOp",EDGE,"E77.right"),sQuery(id+"F4.wireOp",EDGE,"E78.bottom"),sQuery(id+"F4.wireOp",EDGE,"E78.top"),sQuery(id+"F4.wireOp",EDGE,"E78.right"),sQuery(id+"F4.wireOp",EDGE,"E79.bottom"),sQuery(id+"F4.wireOp",EDGE,"E79.top"),sQuery(id+"F4.wireOp",EDGE,"E80.top"),sQuery(id+"F4.wireOp",EDGE,"E80.left"),sQuery(id+"F4.wireOp",EDGE,"E80.right"),sQuery(id+"F4.wireOp",EDGE,"E81.bottom"),sQuery(id+"F4.wireOp",EDGE,"E81.top"),sQuery(id+"F4.wireOp",EDGE,"E81.right"),sQuery(id+"F4.wireOp",EDGE,"E82.bottom"),sQuery(id+"F4.wireOp",EDGE,"E82.top"),sQuery(id+"F4.wireOp",EDGE,"E83.bottom"),sQuery(id+"F4.wireOp",EDGE,"E83.top"),sQuery(id+"F4.wireOp",EDGE,"E83.right"),sQuery(id+"F4.wireOp",EDGE,"E84.top"),sQuery(id+"F4.wireOp",EDGE,"E84.left"),sQuery(id+"F4.wireOp",EDGE,"E84.right"),sQuery(id+"F4.wireOp",EDGE,"E85"),sQuery(id+"F4.wireOp",EDGE,"E86"),sQuery(id+"F4.wireOp",EDGE,"E87"),sQuery(id+"F4.wireOp",EDGE,"E88.bottom"),sQuery(id+"F4.wireOp",EDGE,"E88.top"),sQuery(id+"F4.wireOp",EDGE,"E88.left"),sQuery(id+"F4.wireOp",EDGE,"E88.right"),sQuery(id+"F4.wireOp",EDGE,"E89.top"),sQuery(id+"F4.wireOp",EDGE,"E89.left"),sQuery(id+"F4.wireOp",EDGE,"E89.right"),sQuery(id+"F4.wireOp",EDGE,"E90.bottom"),sQuery(id+"F4.wireOp",EDGE,"E90.top"),sQuery(id+"F4.wireOp",EDGE,"E90.left"),sQuery(id+"F4.wireOp",EDGE,"E90.right"),sQuery(id+"F4.wireOp",EDGE,"E91.left"),sQuery(id+"F4.wireOp",EDGE,"E91.right"),sQuery(id+"F4.wireOp",EDGE,"E92.bottom"),sQuery(id+"F4.wireOp",EDGE,"E92.top"),sQuery(id+"F4.wireOp",EDGE,"E92.left"),sQuery(id+"F4.wireOp",EDGE,"E92.right"),sQuery(id+"F4.wireOp",EDGE,"E93.bottom"),sQuery(id+"F4.wireOp",EDGE,"E93.left"),sQuery(id+"F4.wireOp",EDGE,"E93.right"),sQuery(id+"F4.wireOp",EDGE,"E100.bottom"),sQuery(id+"F4.wireOp",EDGE,"E100.top"),sQuery(id+"F4.wireOp",EDGE,"E100.right"),sQuery(id+"F4.wireOp",EDGE,"E101.left"),sQuery(id+"F4.wireOp",EDGE,"E101.right"),sQuery(id+"F4.wireOp",EDGE,"E102"),sQuery(id+"F4.wireOp",EDGE,"E103"),sQuery(id+"F4.wireOp",EDGE,"E104.bottom"),sQuery(id+"F4.wireOp",EDGE,"E104.top"),sQuery(id+"F4.wireOp",EDGE,"E105.bottom"),sQuery(id+"F4.wireOp",EDGE,"E105.top")])],"isStart":false}),makeQuery(id+"F13.opExtrude","CAP_FACE",FACE,{"disambiguationData":[OSD([sQuery(id+"F12.wireOp",EDGE,"E119.bottom"),sQuery(id+"F12.wireOp",EDGE,"E119.top"),sQuery(id+"F12.wireOp",EDGE,"E119.left"),sQuery(id+"F12.wireOp",EDGE,"E119.right")])],"isStart":false})]}),makeQuery(id+"F15.opExtrude","CAP_FACE",FACE,{"disambiguationData":[OSD([sQuery(id+"F14.wireOp",EDGE,"E121.bottom"),sQuery(id+"F14.wireOp",EDGE,"E121.top"),sQuery(id+"F14.wireOp",EDGE,"E121.left"),sQuery(id+"F14.wireOp",EDGE,"E121.right")])],"isStart":false})]}),makeQuery(id+"F23.opExtrude","CAP_FACE",FACE,{"disambiguationData":[OSD([sQuery(id+"F22.wireOp",EDGE,"E130.bottom"),sQuery(id+"F22.wireOp",EDGE,"E130.top"),sQuery(id+"F22.wireOp",EDGE,"E130.right"),sQuery(id+"F22.wireOp",EDGE,"E131.bottom"),sQuery(id+"F22.wireOp",EDGE,"E131.top"),sQuery(id+"F22.wireOp",EDGE,"E131.right"),sQuery(id+"F22.wireOp",EDGE,"E132.bottom"),sQuery(id+"F22.wireOp",EDGE,"E132.top"),sQuery(id+"F22.wireOp",EDGE,"E133.bottom"),sQuery(id+"F22.wireOp",EDGE,"E133.top"),sQuery(id+"F22.wireOp",EDGE,"E133.left"),sQuery(id+"F22.wireOp",EDGE,"E133.right"),sQuery(id+"F22.wireOp",EDGE,"E134.bottom"),sQuery(id+"F22.wireOp",EDGE,"E134.top"),sQuery(id+"F22.wireOp",EDGE,"E134.right")])],"isStart":false})]});
            var sketch = newSketch(context, id + "F30", { "sketchPlane" : qUnion([Q0])});
            skLineSegment(sketch, "E155.bottom", {"start": v(-49.92, -24.49) * mm, "end": v(-40.91, -24.49) * mm});
            skLineSegment(sketch, "E155.top", {"start": v(-49.92, -25.96) * mm, "end": v(-40.91, -25.96) * mm});
            skLineSegment(sketch, "E155.left", {"start": v(-49.92, -24.49) * mm, "end": v(-49.92, -25.96) * mm});
            skLineSegment(sketch, "E155.right", {"start": v(-40.91, -24.49) * mm, "end": v(-40.91, -25.96) * mm});
            skPoint(sketch, "E156.oppositeSnap0", {"position": v(-30.91, -27.79) * mm});
            skLineSegment(sketch, "E156.bottom", {"start": v(-32.37, -25.96) * mm, "end": v(-30.91, -25.96) * mm});
            skLineSegment(sketch, "E156.top", {"start": v(-32.37, -37.51) * mm, "end": v(-30.91, -37.51) * mm});
            skLineSegment(sketch, "E156.left", {"start": v(-32.37, -25.96) * mm, "end": v(-32.37, -37.51) * mm});
            skLineSegment(sketch, "E156.right", {"start": v(-30.91, -25.96) * mm, "end": v(-30.91, -37.51) * mm});
            skLineSegment(sketch, "E157.bottom", {"start": v(-20.83, -35.99) * mm, "end": v(-30.91, -35.99) * mm});
            skLineSegment(sketch, "E157.top", {"start": v(-20.83, -37.51) * mm, "end": v(-30.91, -37.51) * mm});
            skLineSegment(sketch, "E157.left", {"start": v(-20.83, -35.99) * mm, "end": v(-20.83, -37.51) * mm});
            skLineSegment(sketch, "E157.right", {"start": v(-30.91, -35.99) * mm, "end": v(-30.91, -37.51) * mm});
            skLineSegment(sketch, "E158.bottom", {"start": v(1.22, -30.48) * mm, "end": v(-6.82, -30.48) * mm});
            skLineSegment(sketch, "E158.top", {"start": v(1.22, -33.13) * mm, "end": v(-6.82, -33.13) * mm});
            skLineSegment(sketch, "E158.left", {"start": v(1.22, -30.48) * mm, "end": v(1.22, -33.13) * mm});
            skLineSegment(sketch, "E158.right", {"start": v(-6.82, -30.48) * mm, "end": v(-6.82, -33.13) * mm});
            skLineSegment(sketch, "E159.bottom", {"start": v(17, -34.9) * mm, "end": v(11.66, -34.9) * mm});
            skLineSegment(sketch, "E159.top", {"start": v(17, -33.79) * mm, "end": v(11.66, -33.79) * mm});
            skLineSegment(sketch, "E159.left", {"start": v(17, -34.9) * mm, "end": v(17, -33.79) * mm});
            skLineSegment(sketch, "E159.right", {"start": v(11.66, -34.9) * mm, "end": v(11.66, -33.79) * mm});
            skSolve(sketch);
        }
        {
            var Q0;
            Q0 = qSketchRegion(id + "F30", true);
            extrude(context, id + "F31", {"entities" : qUnion([Q0]), "operationType" : NewBodyOperationType.REMOVE, "oppositeDirection" : true, "depth" : 15 * mm, "offsetDistance" : 25 * mm});
        }
        {
            var Q0;
            Q0=makeQuery(id+"F5.opExtrude","SWEPT_FACE",FACE,{"disambiguationData":[OSD([sQuery(id+"F4.wireOp",EDGE,"E30.left"),sQuery(id+"F4.wireOp",EDGE,"E31.left")])]});
            var sketch = newSketch(context, id + "F32", { "sketchPlane" : qUnion([Q0])});
            skLineSegment(sketch, "E160.bottom", {"start": v(15.57, 19.3) * mm, "end": v(27.89, 19.3) * mm});
            skLineSegment(sketch, "E160.top", {"start": v(15.57, 12) * mm, "end": v(27.89, 12) * mm});
            skLineSegment(sketch, "E160.left", {"start": v(15.57, 19.3) * mm, "end": v(15.57, 12) * mm});
            skLineSegment(sketch, "E160.right", {"start": v(27.89, 19.3) * mm, "end": v(27.89, 12) * mm});
            skSolve(sketch);
        }
        {
            var Q0;
            Q0 = qSketchRegion(id + "F32", true);
            extrude(context, id + "F33", {"entities" : qUnion([Q0]), "operationType" : NewBodyOperationType.ADD, "depth" : 0.5 * mm, "offsetDistance" : 25 * mm});
        }
        {
            var Q0;
            Q0=qCreatedBy(makeId("Top.planeOp"),FACE);
            var sketch = newSketch(context, id + "F34", { "sketchPlane" : qUnion([Q0])});
            skLineSegment(sketch, "E161.bottom", {"start": v(-47.3, -24.5) * mm, "end": v(-43.55, -24.5) * mm});
            skLineSegment(sketch, "E161.left", {"start": v(-47.3, -24.5) * mm, "end": v(-47.3, -19.64) * mm});
            skLineSegment(sketch, "E161.right", {"start": v(-43.55, -24.5) * mm, "end": v(-43.55, -19.64) * mm});
            skArc(sketch, "E162", {"start": v(-43.55, -19.64) * mm, "mid": v(-45.43, -17.76) * mm, "end": v(-47.3, -19.64) * mm});
            skLineSegment(sketch, "E163.bottom", {"start": v(7.18, -15.32) * mm, "end": v(2.38, -15.32) * mm});
            skLineSegment(sketch, "E163.top", {"start": v(7.18, -19.09) * mm, "end": v(2.38, -19.09) * mm});
            skLineSegment(sketch, "E163.left", {"start": v(7.18, -15.32) * mm, "end": v(7.18, -19.09) * mm});
            skArc(sketch, "E164", {"start": v(2.38, -15.32) * mm, "mid": v(0.5, -17.2) * mm, "end": v(2.38, -19.09) * mm});
            skSolve(sketch);
        }
        {
            var Q0;
            Q0 = qSketchRegion(id + "F34", true);
            extrude(context, id + "F35", {"entities" : qUnion([Q0]), "operationType" : NewBodyOperationType.ADD, "depth" : 4 * mm, "offsetDistance" : 25 * mm});
        }
        {
            var Q0;
            Q0=qCreatedBy(makeId("Top.planeOp"),FACE);
            var sketch = newSketch(context, id + "F36", { "sketchPlane" : qUnion([Q0])});
            skLineSegment(sketch, "E165.bottom", {"start": v(-40.94, -18.95) * mm, "end": v(-31.77, -18.95) * mm});
            skLineSegment(sketch, "E165.top", {"start": v(-40.94, -24.5) * mm, "end": v(-31.77, -24.5) * mm});
            skLineSegment(sketch, "E165.left", {"start": v(-40.94, -18.95) * mm, "end": v(-40.94, -24.5) * mm});
            skLineSegment(sketch, "E165.right", {"start": v(-31.77, -18.95) * mm, "end": v(-31.77, -24.5) * mm});
            skLineSegment(sketch, "E166.bottom", {"start": v(7.22, -6.34) * mm, "end": v(1.63, -6.34) * mm});
            skLineSegment(sketch, "E166.top", {"start": v(7.22, -13.55) * mm, "end": v(1.63, -13.55) * mm});
            skLineSegment(sketch, "E166.left", {"start": v(7.22, -6.34) * mm, "end": v(7.22, -13.55) * mm});
            skLineSegment(sketch, "E166.right", {"start": v(1.63, -6.34) * mm, "end": v(1.63, -13.55) * mm});
            skSolve(sketch);
        }
        {
            var Q0;
            Q0 = qSketchRegion(id + "F36", true);
            extrude(context, id + "F37", {"entities" : qUnion([Q0]), "operationType" : NewBodyOperationType.ADD, "depth" : 12 * mm, "offsetDistance" : 25 * mm});
        }
        {
            var Q0;
            Q0=makeQuery(id+"F37.boolean.opBoolean","MERGE",FACE,{"derivedFrom":[makeQuery(id+"F31.boolean.opBoolean","COPY",FACE,{"derivedFrom":makeQuery(id+"F31.opExtrude","CAP_FACE",FACE,{"disambiguationData":[OSD([sQuery(id+"F30.wireOp",EDGE,"E155.bottom"),sQuery(id+"F30.wireOp",EDGE,"E155.top"),sQuery(id+"F30.wireOp",EDGE,"E155.left"),sQuery(id+"F30.wireOp",EDGE,"E155.right")])],"isStart":false})}),makeQuery(id+"F37.opExtrude","CAP_FACE",FACE,{"disambiguationData":[OSD([sQuery(id+"F36.wireOp",EDGE,"E165.bottom"),sQuery(id+"F36.wireOp",EDGE,"E165.top"),sQuery(id+"F36.wireOp",EDGE,"E165.left"),sQuery(id+"F36.wireOp",EDGE,"E165.right")])],"isStart":false})]});
            var sketch = newSketch(context, id + "F38", { "sketchPlane" : qUnion([Q0])});
            skLineSegment(sketch, "E167.bottom", {"start": v(-39.07, -19.45) * mm, "end": v(-33.74, -19.45) * mm});
            skLineSegment(sketch, "E167.top", {"start": v(-39.07, -23.21) * mm, "end": v(-33.74, -23.21) * mm});
            skLineSegment(sketch, "E167.left", {"start": v(-39.07, -19.45) * mm, "end": v(-39.07, -23.21) * mm});
            skLineSegment(sketch, "E167.right", {"start": v(-33.74, -19.45) * mm, "end": v(-33.74, -23.21) * mm});
            skLineSegment(sketch, "E168.bottom", {"start": v(6.07, -7.27) * mm, "end": v(2.24, -7.27) * mm});
            skLineSegment(sketch, "E168.top", {"start": v(6.07, -12.5) * mm, "end": v(2.24, -12.5) * mm});
            skLineSegment(sketch, "E168.left", {"start": v(6.07, -7.27) * mm, "end": v(6.07, -12.5) * mm});
            skLineSegment(sketch, "E168.right", {"start": v(2.24, -7.27) * mm, "end": v(2.24, -12.5) * mm});
            skSolve(sketch);
        }
        {
            var Q0;
            Q0=makeQuery(id+"F38.imprint","IMPRINT",FACE,{"disambiguationData":[TD([[makeQuery(id+"F38.imprint","IMPRINT",EDGE,{"derivedFrom":sQuery(id+"F38.wireOp",EDGE,"E167.bottom")}),-1.0]])]});
            var Q1;
            Q1=makeQuery(id+"F38.imprint","IMPRINT",FACE,{"disambiguationData":[TD([[makeQuery(id+"F38.imprint","IMPRINT",EDGE,{"derivedFrom":sQuery(id+"F38.wireOp",EDGE,"E168.bottom")}),1.0]])]});
            extrude(context, id + "F39", {"entities" : qUnion([Q0, Q1]), "operationType" : NewBodyOperationType.REMOVE, "oppositeDirection" : true, "depth" : 2.5 * mm, "offsetDistance" : 25 * mm});
        }
        {
            var Q0;
            Q0=makeQuery(id+"F29.opExtrude","CAP_FACE",FACE,{"disambiguationData":[OSD([sQuery(id+"F28.wireOp",EDGE,"E149.left"),sQuery(id+"F28.wireOp",EDGE,"E150.MirrorCS"),sQuery(id+"F28.wireOp",EDGE,"E151.MirrorCS"),sQuery(id+"F28.wireOp",EDGE,"E152.MirrorCS"),sQuery(id+"F28.wireOp",EDGE,"E153.filletArc"),sQuery(id+"F28.wireOp",EDGE,"E154.filletArc")])],"isStart":false});
            var sketch = newSketch(context, id + "F40", { "sketchPlane" : qUnion([Q0])});
            skLineSegment(sketch, "E169.bottom", {"start": v(50.89, 30.51) * mm, "end": v(57.09, 30.51) * mm});
            skLineSegment(sketch, "E169.top", {"start": v(50.89, 13.68) * mm, "end": v(57.09, 13.68) * mm});
            skLineSegment(sketch, "E169.left", {"start": v(50.89, 30.51) * mm, "end": v(50.89, 13.68) * mm});
            skLineSegment(sketch, "E169.right", {"start": v(57.09, 30.51) * mm, "end": v(57.09, 13.68) * mm});
            skSolve(sketch);
        }
        {
            var Q0;
            Q0=makeQuery(id+"F40.imprint","IMPRINT",FACE,{"disambiguationData":[TD([[makeQuery(id+"F40.imprint","IMPRINT",EDGE,{"derivedFrom":sQuery(id+"F40.wireOp",EDGE,"E169.bottom")}),-1.0]])]});
            extrude(context, id + "F41", {"entities" : qUnion([Q0]), "operationType" : NewBodyOperationType.REMOVE, "oppositeDirection" : true, "depth" : 4 * mm, "offsetDistance" : 25 * mm});
        }
        {
            var Q0;
            Q0=makeQuery(id+"F41.boolean.opBoolean","COPY",FACE,{"derivedFrom":makeQuery(id+"F41.opExtrude","SWEPT_FACE",FACE,{"disambiguationData":[OSD([sQuery(id+"F40.wireOp",EDGE,"E169.bottom")])]})});
            var Q1;
            Q1=makeQuery(id+"F41.boolean.opBoolean","COPY",FACE,{"derivedFrom":makeQuery(id+"F41.opExtrude","SWEPT_FACE",FACE,{"disambiguationData":[OSD([sQuery(id+"F40.wireOp",EDGE,"E169.top")])]})});
            var Q2;
            Q2=makeQuery(id+"F41.boolean.opBoolean","COPY",EDGE,{"derivedFrom":makeQuery(id+"F41.opExtrude","CAP_EDGE",EDGE,{"disambiguationData":[OSD([sQuery(id+"F40.wireOp",EDGE,"E169.right")])],"isStart":false})});
            var Q3;
            Q3=makeQuery(id+"F29.opExtrude","CAP_EDGE",EDGE,{"disambiguationData":[OSD([sQuery(id+"F28.wireOp",EDGE,"E150.MirrorCS")])],"isStart":false});
            var Q4;
            Q4=makeQuery(id+"F29.opExtrude","CAP_EDGE",EDGE,{"disambiguationData":[OSD([sQuery(id+"F28.wireOp",EDGE,"E152.MirrorCS")])],"isStart":false});
            fillet(context, id + "F42", {"entities" : qUnion([Q0, Q1, Q2, Q3, Q4]), "radius" : 1 * mm, "tangentPropagation" : true, "allowEdgeOverflow" : false});
        }
        {
            var Q0;
            Q0=qCreatedBy(makeId("Top.planeOp"),FACE);
            cPlane(context, id + "F43", {"entities" : qUnion([Q0]), "cplaneType" : CPlaneType.OFFSET, "offset" : 27 * mm, "width" : 150 * mm, "height" : 150 * mm});
        }
        {
            var Q0;
            Q0=qCreatedBy(id+"F43.planeOp",FACE);
            var sketch = newSketch(context, id + "F44", { "sketchPlane" : qUnion([Q0])});
            skCircle(sketch, "E170", {"center": v(-46.03, 22.08) * mm, "radius": 7.5 * mm});
            skCircle(sketch, "E171", {"center": v(-15.58, 24) * mm, "radius": 6 * mm});
            skCircle(sketch, "E172", {"center": v(10.16, 24.24) * mm, "radius": 6 * mm});
            skCircle(sketch, "E173", {"center": v(40.3, 21.07) * mm, "radius": 7.5 * mm});
            skCircle(sketch, "E174", {"center": v(52.39, -4.3) * mm, "radius": 6 * mm});
            skCircle(sketch, "E175", {"center": v(-18.91, -24.99) * mm, "radius": 6 * mm});
            skSolve(sketch);
        }
        {
            var Q0;
            Q0 = qSketchRegion(id + "F44", true);
            extrude(context, id + "F45", {"entities" : qUnion([Q0]), "oppositeDirection" : true, "depth" : 3 * mm, "offsetDistance" : 25 * mm});
        }
        {
            var Q0;
            {var subQ166=sQuery(id+"F2.wireOp",EDGE,"E9");var subQ170=sQuery(id+"F2.wireOp",EDGE,"E8");var subQ175=sQuery(id+"F2.wireOp",EDGE,"E7");var subQ189=sQuery(id+"F2.wireOp",EDGE,"E6");var subQ205=sQuery(id+"F2.wireOp",EDGE,"E5");var subQ217=sQuery(id+"F2.wireOp",EDGE,"E10");var subQ229=sQuery(id+"F2.wireOp",EDGE,"E1");var subQ230=makeQuery(id+"F3.opExtrude","SWEPT_FACE",FACE,{"disambiguationData":[OSD([subQ229])]});var subQ233=sQuery(id+"F2.wireOp",EDGE,"E4");var subQ280=sQuery(id+"F2.wireOp",EDGE,"E2");var subQ284=sQuery(id+"F2.wireOp",EDGE,"E3");var subQ289=sQuery(id+"F2.wireOp",EDGE,"E12");var subQ293=sQuery(id+"F2.wireOp",EDGE,"E14");var subQ333=sQuery(id+"F2.wireOp",EDGE,"E13");var subQ334=sQuery(id+"F2.wireOp",EDGE,"E11");Q0=makeQuery(id+"F31.boolean.opBoolean","MERGE",FACE,{"derivedFrom":[makeQuery(id+"F23.boolean.opBoolean","SPLIT",FACE,{"disambiguationData":[TD([subQ230])],"derivedFrom":makeQuery(id+"F5.boolean.opBoolean","SPLIT",FACE,{"disambiguationData":[TD([subQ230])],"derivedFrom":makeQuery(id+"F3.opExtrude","CAP_FACE",FACE,{"disambiguationData":[OSD([subQ229,subQ280,subQ284,subQ233,subQ205,subQ189,subQ175,subQ170,subQ166,subQ217,subQ334,subQ289,subQ333,subQ293])],"isStart":true})})})],"fromTools":[makeQuery(id+"F31.opExtrude","CAP_FACE",FACE,{"disambiguationData":[OSD([sQuery(id+"F30.wireOp",EDGE,"E155.bottom"),sQuery(id+"F30.wireOp",EDGE,"E155.top"),sQuery(id+"F30.wireOp",EDGE,"E155.left"),sQuery(id+"F30.wireOp",EDGE,"E155.right")])],"isStart":false}),makeQuery(id+"F31.opExtrude","CAP_FACE",FACE,{"disambiguationData":[OSD([sQuery(id+"F30.wireOp",EDGE,"E156.bottom"),sQuery(id+"F30.wireOp",EDGE,"E156.top"),sQuery(id+"F30.wireOp",EDGE,"E156.left"),sQuery(id+"F30.wireOp",EDGE,"E156.right"),sQuery(id+"F30.wireOp",EDGE,"E157.bottom"),sQuery(id+"F30.wireOp",EDGE,"E157.top"),sQuery(id+"F30.wireOp",EDGE,"E157.left")])],"isStart":false}),makeQuery(id+"F31.opExtrude","CAP_FACE",FACE,{"disambiguationData":[OSD([sQuery(id+"F30.wireOp",EDGE,"E158.bottom"),sQuery(id+"F30.wireOp",EDGE,"E158.top"),sQuery(id+"F30.wireOp",EDGE,"E158.left"),sQuery(id+"F30.wireOp",EDGE,"E158.right")])],"isStart":false}),makeQuery(id+"F31.opExtrude","CAP_FACE",FACE,{"disambiguationData":[OSD([sQuery(id+"F30.wireOp",EDGE,"E159.bottom"),sQuery(id+"F30.wireOp",EDGE,"E159.top"),sQuery(id+"F30.wireOp",EDGE,"E159.left"),sQuery(id+"F30.wireOp",EDGE,"E159.right")])],"isStart":false})]});}
            var sketch = newSketch(context, id + "F46", { "sketchPlane" : qUnion([Q0])});
            skLineSegment(sketch, "E176.bottom", {"start": v(-50.6, 13.08) * mm, "end": v(-37.9, 13.08) * mm});
            skLineSegment(sketch, "E176.top", {"start": v(-50.6, 5.46) * mm, "end": v(-37.9, 5.46) * mm});
            skLineSegment(sketch, "E176.left", {"start": v(-50.6, 13.08) * mm, "end": v(-50.6, 5.46) * mm});
            skLineSegment(sketch, "E176.right", {"start": v(-37.9, 13.08) * mm, "end": v(-37.9, 5.46) * mm});
            skSolve(sketch);
        }
        {
            var Q0;
            Q0=makeQuery(id+"F46.imprint","IMPRINT",FACE,{"disambiguationData":[TD([[makeQuery(id+"F46.imprint","IMPRINT",EDGE,{"derivedFrom":sQuery(id+"F46.wireOp",EDGE,"E176.bottom")}),-1.0]])]});
            var Q1;
            Q1 = qSketchRegion(id + "F46", true);
            extrude(context, id + "F47", {"entities" : qUnion([Q0, Q1]), "operationType" : NewBodyOperationType.ADD, "depth" : 10 * mm, "offsetDistance" : 25 * mm});
        }
        {
            var Q0;
            Q0=qCreatedBy(id+"F43.planeOp",FACE);
            var sketch = newSketch(context, id + "F48", { "sketchPlane" : qUnion([Q0])});
            skLineSegment(sketch, "E177.bottom", {"start": v(-49.2, -11.9) * mm, "end": v(-46.63, -11.9) * mm});
            skLineSegment(sketch, "E177.top", {"start": v(-49.2, -14.35) * mm, "end": v(-46.63, -14.35) * mm});
            skLineSegment(sketch, "E177.left", {"start": v(-49.2, -11.9) * mm, "end": v(-49.2, -14.35) * mm});
            skLineSegment(sketch, "E177.right", {"start": v(-46.63, -11.9) * mm, "end": v(-46.63, -14.35) * mm});
            skLineSegment(sketch, "E178.bottom", {"start": v(-3.26, -19.12) * mm, "end": v(-0.81, -19.12) * mm});
            skLineSegment(sketch, "E178.top", {"start": v(-3.26, -22.09) * mm, "end": v(-0.81, -22.09) * mm});
            skLineSegment(sketch, "E178.left", {"start": v(-3.26, -19.12) * mm, "end": v(-3.26, -22.09) * mm});
            skLineSegment(sketch, "E178.right", {"start": v(-0.81, -19.12) * mm, "end": v(-0.81, -22.09) * mm});
            skLineSegment(sketch, "E179.bottom", {"start": v(21.51, -20.02) * mm, "end": v(25.39, -20.02) * mm});
            skLineSegment(sketch, "E179.top", {"start": v(21.51, -23.5) * mm, "end": v(25.39, -23.5) * mm});
            skLineSegment(sketch, "E179.left", {"start": v(21.51, -20.02) * mm, "end": v(21.51, -23.5) * mm});
            skLineSegment(sketch, "E179.right", {"start": v(25.39, -20.02) * mm, "end": v(25.39, -23.5) * mm});
            skLineSegment(sketch, "E180.bottom", {"start": v(0.1, 0.5) * mm, "end": v(3.45, 0.5) * mm});
            skLineSegment(sketch, "E180.top", {"start": v(0.1, -1.83) * mm, "end": v(3.45, -1.83) * mm});
            skLineSegment(sketch, "E180.left", {"start": v(0.1, 0.5) * mm, "end": v(0.1, -1.83) * mm});
            skLineSegment(sketch, "E180.right", {"start": v(3.45, 0.5) * mm, "end": v(3.45, -1.83) * mm});
            skLineSegment(sketch, "E181.bottom", {"start": v(18.16, -45.19) * mm, "end": v(20.61, -45.19) * mm});
            skLineSegment(sketch, "E181.top", {"start": v(18.16, -46.6) * mm, "end": v(20.61, -46.6) * mm});
            skLineSegment(sketch, "E181.left", {"start": v(18.16, -45.19) * mm, "end": v(18.16, -46.6) * mm});
            skLineSegment(sketch, "E181.right", {"start": v(20.61, -45.19) * mm, "end": v(20.61, -46.6) * mm});
            skLineSegment(sketch, "E182.bottom", {"start": v(30.94, -45.45) * mm, "end": v(32.61, -45.45) * mm});
            skLineSegment(sketch, "E182.top", {"start": v(30.94, -46.87) * mm, "end": v(32.61, -46.87) * mm});
            skLineSegment(sketch, "E182.left", {"start": v(30.94, -45.45) * mm, "end": v(30.94, -46.87) * mm});
            skLineSegment(sketch, "E182.right", {"start": v(32.61, -45.45) * mm, "end": v(32.61, -46.87) * mm});
            skLineSegment(sketch, "E183.bottom", {"start": v(47.71, -43.12) * mm, "end": v(50.3, -43.12) * mm});
            skLineSegment(sketch, "E183.top", {"start": v(47.71, -45.32) * mm, "end": v(50.3, -45.32) * mm});
            skLineSegment(sketch, "E183.left", {"start": v(47.71, -43.12) * mm, "end": v(47.71, -45.32) * mm});
            skLineSegment(sketch, "E183.right", {"start": v(50.3, -43.12) * mm, "end": v(50.3, -45.32) * mm});
            skLineSegment(sketch, "E184.bottom", {"start": v(49.65, -26.35) * mm, "end": v(52.1, -26.35) * mm});
            skLineSegment(sketch, "E184.top", {"start": v(49.65, -28.8) * mm, "end": v(52.1, -28.8) * mm});
            skLineSegment(sketch, "E184.left", {"start": v(49.65, -26.35) * mm, "end": v(49.65, -28.8) * mm});
            skLineSegment(sketch, "E184.right", {"start": v(52.1, -26.35) * mm, "end": v(52.1, -28.8) * mm});
            skSolve(sketch);
        }
        {
            var Q0;
            Q0 = qSketchRegion(id + "F48", true);
            extrude(context, id + "F49", {"entities" : qUnion([Q0]), "oppositeDirection" : true, "depth" : 1 * mm, "offsetDistance" : 25 * mm});
        }
    });
